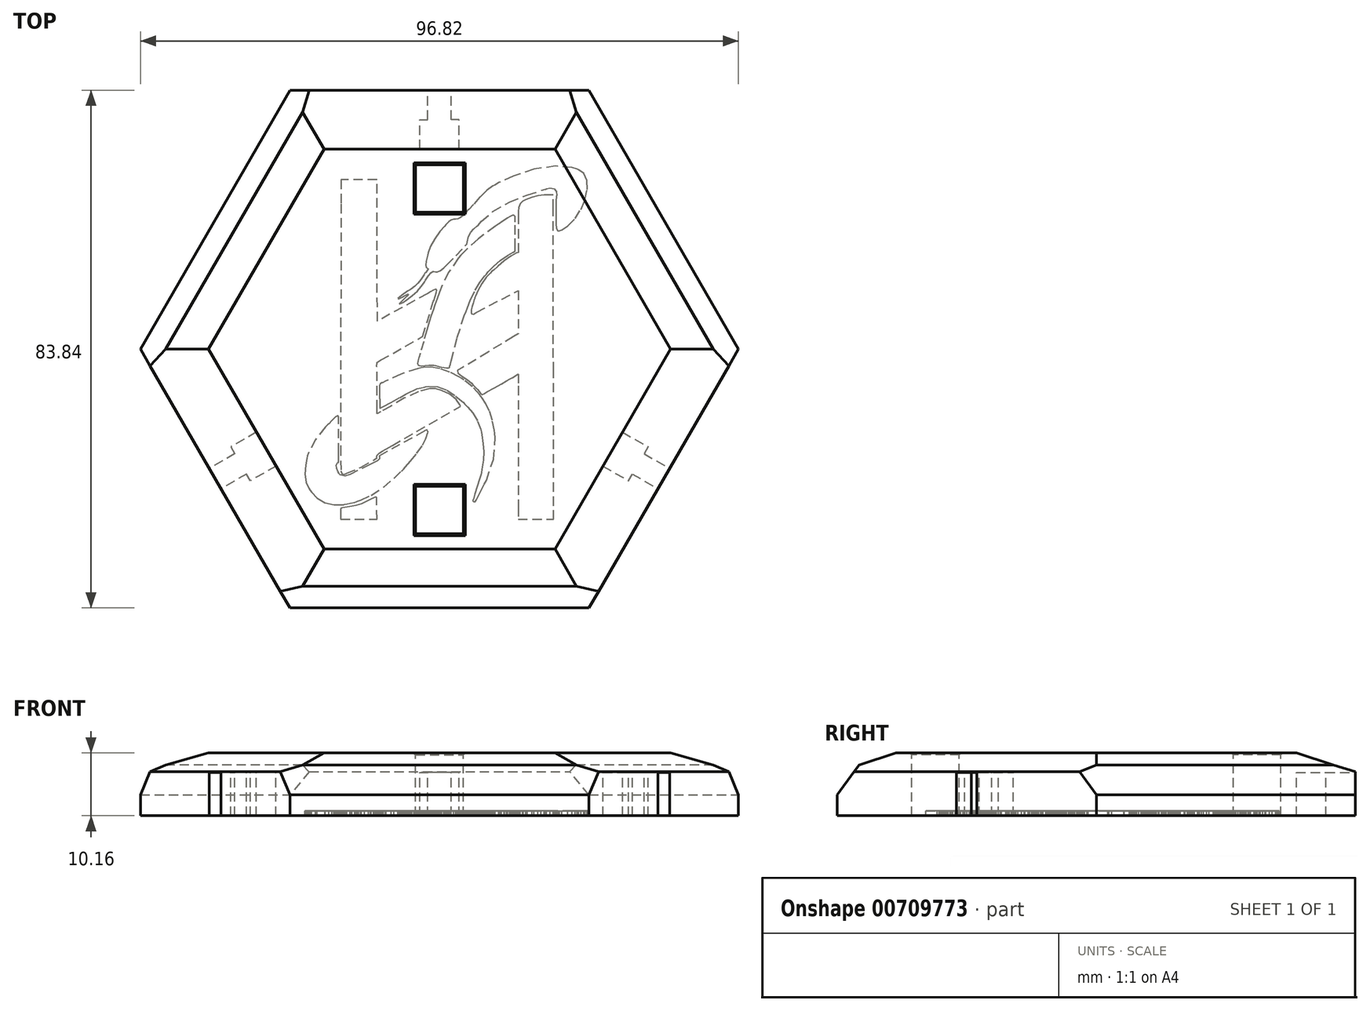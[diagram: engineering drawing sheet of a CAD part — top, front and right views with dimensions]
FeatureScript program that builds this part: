
annotation { "Feature Type Name" : "Feature", "Feature Type Description" : "" }
export const myFeature = defineFeature(function(context is Context, id is Id, definition is map)
    precondition{}
    {
        {
            var Q0;
            Q0=qCreatedBy(makeId("Top.planeOp"),FACE);
            var sketch = newSketch(context, id + "F0", { "sketchPlane" : qUnion([Q0])});
            skLineSegment(sketch, "E0", {"start": v(-18.44, -1.4) * mm, "end": v(-18.44, 0.8) * mm});
            skLineSegment(sketch, "E1", {"start": v(-18.44, 0.8) * mm, "end": v(-18.42, 22.77) * mm});
            skLineSegment(sketch, "E2", {"start": v(-18.42, 22.77) * mm, "end": v(-18.4, 24.97) * mm});
            skLineSegment(sketch, "E3", {"start": v(-18.4, 24.97) * mm, "end": v(-18.04, 24.97) * mm});
            skLineSegment(sketch, "E4", {"start": v(-18.04, 24.97) * mm, "end": v(-16.92, 24.95) * mm});
            skLineSegment(sketch, "E5", {"start": v(-16.92, 24.95) * mm, "end": v(-15.91, 24.86) * mm});
            skLineSegment(sketch, "E6", {"start": v(-15.91, 24.86) * mm, "end": v(-14.95, 24.59) * mm});
            skLineSegment(sketch, "E7", {"start": v(-14.95, 24.59) * mm, "end": v(-13.94, 24.18) * mm});
            skLineSegment(sketch, "E8", {"start": v(-13.94, 24.18) * mm, "end": v(-13.6, 24.04) * mm});
            skLineSegment(sketch, "E9", {"start": v(-13.6, 24.04) * mm, "end": v(-13.45, 23.96) * mm});
            skLineSegment(sketch, "E10", {"start": v(-13.45, 23.96) * mm, "end": v(-13.07, 23.56) * mm});
            skLineSegment(sketch, "E11", {"start": v(-13.07, 23.56) * mm, "end": v(-12.83, 22.93) * mm});
            skLineSegment(sketch, "E12", {"start": v(-12.83, 22.93) * mm, "end": v(-12.77, 22.28) * mm});
            skLineSegment(sketch, "E13", {"start": v(-12.77, 22.28) * mm, "end": v(-12.78, 21.88) * mm});
            skLineSegment(sketch, "E14", {"start": v(-12.78, 21.88) * mm, "end": v(-12.77, 21.74) * mm});
            skLineSegment(sketch, "E15", {"start": v(-12.77, 21.74) * mm, "end": v(-12.77, 15.65) * mm});
            skLineSegment(sketch, "E16", {"start": v(-12.77, 15.65) * mm, "end": v(-12.46, 15.54) * mm});
            skLineSegment(sketch, "E17", {"start": v(-12.46, 15.54) * mm, "end": v(-11.56, 15.07) * mm});
            skLineSegment(sketch, "E18", {"start": v(-11.56, 15.07) * mm, "end": v(-10.49, 14.3) * mm});
            skLineSegment(sketch, "E19", {"start": v(-10.49, 14.3) * mm, "end": v(-9.48, 13.42) * mm});
            skLineSegment(sketch, "E20", {"start": v(-9.48, 13.42) * mm, "end": v(-8.73, 12.77) * mm});
            skLineSegment(sketch, "E21", {"start": v(-8.73, 12.77) * mm, "end": v(-8.47, 12.56) * mm});
            skLineSegment(sketch, "E22", {"start": v(-8.47, 12.56) * mm, "end": v(-8.23, 12.35) * mm});
            skLineSegment(sketch, "E23", {"start": v(-8.23, 12.35) * mm, "end": v(-7.57, 11.64) * mm});
            skLineSegment(sketch, "E24", {"start": v(-7.57, 11.64) * mm, "end": v(-6.85, 10.6) * mm});
            skLineSegment(sketch, "E25", {"start": v(-6.85, 10.6) * mm, "end": v(-6.25, 9.47) * mm});
            skLineSegment(sketch, "E26", {"start": v(-6.25, 9.47) * mm, "end": v(-5.85, 8.6) * mm});
            skLineSegment(sketch, "E27", {"start": v(-5.85, 8.6) * mm, "end": v(-5.73, 8.3) * mm});
            skLineSegment(sketch, "E28", {"start": v(-5.73, 8.3) * mm, "end": v(-5.7, 8.2) * mm});
            skLineSegment(sketch, "E29", {"start": v(-5.7, 8.2) * mm, "end": v(-5.6, 7.92) * mm});
            skLineSegment(sketch, "E30", {"start": v(-5.6, 7.92) * mm, "end": v(-5.43, 7.42) * mm});
            skLineSegment(sketch, "E31", {"start": v(-5.43, 7.42) * mm, "end": v(-5.27, 6.87) * mm});
            skLineSegment(sketch, "E32", {"start": v(-5.27, 6.87) * mm, "end": v(-5.14, 6.36) * mm});
            skLineSegment(sketch, "E33", {"start": v(-5.14, 6.36) * mm, "end": v(-5.11, 5.94) * mm});
            skLineSegment(sketch, "E34", {"start": v(-5.11, 5.94) * mm, "end": v(-5.21, 5.7) * mm});
            skLineSegment(sketch, "E35", {"start": v(-5.21, 5.7) * mm, "end": v(-5.5, 5.69) * mm});
            skLineSegment(sketch, "E36", {"start": v(-5.5, 5.69) * mm, "end": v(-5.9, 5.9) * mm});
            skLineSegment(sketch, "E37", {"start": v(-5.9, 5.9) * mm, "end": v(-6, 6) * mm});
            skLineSegment(sketch, "E38", {"start": v(-6, 6) * mm, "end": v(-12.77, 9.46) * mm});
            skLineSegment(sketch, "E39", {"start": v(-12.77, 9.46) * mm, "end": v(-12.77, 2.48) * mm});
            skLineSegment(sketch, "E40", {"start": v(-12.77, 2.48) * mm, "end": v(-11.97, 2.02) * mm});
            skLineSegment(sketch, "E41", {"start": v(-11.97, 2.02) * mm, "end": v(-7.85, -0.48) * mm});
            skLineSegment(sketch, "E42", {"start": v(-7.85, -0.48) * mm, "end": v(-3.73, -3) * mm});
            skLineSegment(sketch, "E43", {"start": v(-3.73, -3) * mm, "end": v(-2.93, -3.45) * mm});
            skLineSegment(sketch, "E44", {"start": v(-2.93, -3.45) * mm, "end": v(-2.88, -3.5) * mm});
            skLineSegment(sketch, "E45", {"start": v(-2.88, -3.5) * mm, "end": v(-3, -3.86) * mm});
            skLineSegment(sketch, "E46", {"start": v(-3, -3.86) * mm, "end": v(-3.61, -4.35) * mm});
            skLineSegment(sketch, "E47", {"start": v(-3.61, -4.35) * mm, "end": v(-4.5, -4.97) * mm});
            skLineSegment(sketch, "E48", {"start": v(-4.5, -4.97) * mm, "end": v(-5.2, -5.53) * mm});
            skLineSegment(sketch, "E49", {"start": v(-5.2, -5.53) * mm, "end": v(-5.4, -5.75) * mm});
            skLineSegment(sketch, "E50", {"start": v(-5.4, -5.75) * mm, "end": v(-5.6, -5.93) * mm});
            skLineSegment(sketch, "E51", {"start": v(-5.6, -5.93) * mm, "end": v(-6.13, -6.53) * mm});
            skLineSegment(sketch, "E52", {"start": v(-6.13, -6.53) * mm, "end": v(-6.6, -7.1) * mm});
            skLineSegment(sketch, "E53", {"start": v(-6.6, -7.1) * mm, "end": v(-6.94, -7.33) * mm});
            skLineSegment(sketch, "E54", {"start": v(-6.94, -7.33) * mm, "end": v(-7.24, -7.2) * mm});
            skLineSegment(sketch, "E55", {"start": v(-7.24, -7.2) * mm, "end": v(-7.3, -7.14) * mm});
            skLineSegment(sketch, "E56", {"start": v(-7.3, -7.14) * mm, "end": v(-7.7, -6.92) * mm});
            skLineSegment(sketch, "E57", {"start": v(-7.7, -6.92) * mm, "end": v(-8.9, -6.26) * mm});
            skLineSegment(sketch, "E58", {"start": v(-8.9, -6.26) * mm, "end": v(-10.06, -5.62) * mm});
            skLineSegment(sketch, "E59", {"start": v(-10.06, -5.62) * mm, "end": v(-10.87, -5.16) * mm});
            skLineSegment(sketch, "E60", {"start": v(-10.87, -5.16) * mm, "end": v(-11.43, -4.84) * mm});
            skLineSegment(sketch, "E61", {"start": v(-11.43, -4.84) * mm, "end": v(-11.8, -4.61) * mm});
            skLineSegment(sketch, "E62", {"start": v(-11.8, -4.61) * mm, "end": v(-12.1, -4.43) * mm});
            skLineSegment(sketch, "E63", {"start": v(-12.1, -4.43) * mm, "end": v(-12.4, -4.25) * mm});
            skLineSegment(sketch, "E64", {"start": v(-12.4, -4.25) * mm, "end": v(-12.68, -4.08) * mm});
            skLineSegment(sketch, "E65", {"start": v(-12.68, -4.08) * mm, "end": v(-12.77, -4.03) * mm});
            skLineSegment(sketch, "E66", {"start": v(-12.77, -4.03) * mm, "end": v(-12.77, -6) * mm});
            skLineSegment(sketch, "E67", {"start": v(-12.77, -6) * mm, "end": v(-12.75, -25.61) * mm});
            skLineSegment(sketch, "E68", {"start": v(-12.75, -25.61) * mm, "end": v(-12.75, -27.57) * mm});
            skLineSegment(sketch, "E69", {"start": v(-12.75, -27.57) * mm, "end": v(-18.45, -27.57) * mm});
            skLineSegment(sketch, "E70", {"start": v(-18.45, -27.57) * mm, "end": v(-18.45, -25.39) * mm});
            skLineSegment(sketch, "E71", {"start": v(-18.45, -25.39) * mm, "end": v(-18.44, -3.57) * mm});
            skLineSegment(sketch, "E72", {"start": v(-18.44, -3.57) * mm, "end": v(-18.44, -1.4) * mm});
            skLineSegment(sketch, "E73", {"start": v(10.16, -24.07) * mm, "end": v(10.2, -24.02) * mm});
            skLineSegment(sketch, "E74", {"start": v(10.2, -24.02) * mm, "end": v(10.42, -23.96) * mm});
            skLineSegment(sketch, "E75", {"start": v(10.42, -23.96) * mm, "end": v(10.62, -24.06) * mm});
            skLineSegment(sketch, "E76", {"start": v(10.62, -24.06) * mm, "end": v(10.67, -24.09) * mm});
            skLineSegment(sketch, "E77", {"start": v(10.67, -24.09) * mm, "end": v(10.87, -24.2) * mm});
            skLineSegment(sketch, "E78", {"start": v(10.87, -24.2) * mm, "end": v(11.5, -24.52) * mm});
            skLineSegment(sketch, "E79", {"start": v(11.5, -24.52) * mm, "end": v(12.12, -24.83) * mm});
            skLineSegment(sketch, "E80", {"start": v(12.12, -24.83) * mm, "end": v(12.62, -25.06) * mm});
            skLineSegment(sketch, "E81", {"start": v(12.62, -25.06) * mm, "end": v(13.08, -25.22) * mm});
            skLineSegment(sketch, "E82", {"start": v(13.08, -25.22) * mm, "end": v(13.56, -25.34) * mm});
            skLineSegment(sketch, "E83", {"start": v(13.56, -25.34) * mm, "end": v(14.16, -25.46) * mm});
            skLineSegment(sketch, "E84", {"start": v(14.16, -25.46) * mm, "end": v(14.93, -25.6) * mm});
            skLineSegment(sketch, "E85", {"start": v(14.93, -25.6) * mm, "end": v(15.71, -25.74) * mm});
            skLineSegment(sketch, "E86", {"start": v(15.71, -25.74) * mm, "end": v(15.97, -25.78) * mm});
            skLineSegment(sketch, "E87", {"start": v(15.97, -25.78) * mm, "end": v(15.98, -25.98) * mm});
            skLineSegment(sketch, "E88", {"start": v(15.98, -25.98) * mm, "end": v(15.99, -26.56) * mm});
            skLineSegment(sketch, "E89", {"start": v(15.99, -26.56) * mm, "end": v(15.99, -26.68) * mm});
            skLineSegment(sketch, "E90", {"start": v(15.99, -26.68) * mm, "end": v(15.99, -26.79) * mm});
            skLineSegment(sketch, "E91", {"start": v(15.99, -26.79) * mm, "end": v(16, -27.38) * mm});
            skLineSegment(sketch, "E92", {"start": v(16, -27.38) * mm, "end": v(16, -27.57) * mm});
            skLineSegment(sketch, "E93", {"start": v(16, -27.57) * mm, "end": v(10.13, -27.57) * mm});
            skLineSegment(sketch, "E94", {"start": v(10.13, -27.57) * mm, "end": v(10.16, -24.07) * mm});
            skLineSegment(sketch, "E95", {"start": v(13.28, -24.66) * mm, "end": v(12.7, -24.46) * mm});
            skLineSegment(sketch, "E96", {"start": v(12.7, -24.46) * mm, "end": v(11.04, -23.66) * mm});
            skLineSegment(sketch, "E97", {"start": v(11.04, -23.66) * mm, "end": v(9.09, -22.38) * mm});
            skLineSegment(sketch, "E98", {"start": v(9.09, -22.38) * mm, "end": v(7.36, -20.93) * mm});
            skLineSegment(sketch, "E99", {"start": v(7.36, -20.93) * mm, "end": v(6.18, -19.81) * mm});
            skLineSegment(sketch, "E100", {"start": v(6.18, -19.81) * mm, "end": v(5.8, -19.44) * mm});
            skLineSegment(sketch, "E101", {"start": v(5.8, -19.44) * mm, "end": v(5.53, -19.12) * mm});
            skLineSegment(sketch, "E102", {"start": v(5.53, -19.12) * mm, "end": v(4.72, -18.18) * mm});
            skLineSegment(sketch, "E103", {"start": v(4.72, -18.18) * mm, "end": v(3.67, -16.88) * mm});
            skLineSegment(sketch, "E104", {"start": v(3.67, -16.88) * mm, "end": v(2.75, -15.54) * mm});
            skLineSegment(sketch, "E105", {"start": v(2.75, -15.54) * mm, "end": v(2.22, -14.52) * mm});
            skLineSegment(sketch, "E106", {"start": v(2.22, -14.52) * mm, "end": v(2.1, -14.15) * mm});
            skLineSegment(sketch, "E107", {"start": v(2.1, -14.15) * mm, "end": v(2.05, -14.05) * mm});
            skLineSegment(sketch, "E108", {"start": v(2.05, -14.05) * mm, "end": v(1.96, -13.73) * mm});
            skLineSegment(sketch, "E109", {"start": v(1.92, -13.3) * mm, "end": v(2.06, -13.09) * mm});
            skLineSegment(sketch, "E110", {"start": v(2.06, -13.09) * mm, "end": v(2.35, -13.21) * mm});
            skLineSegment(sketch, "E111", {"start": v(2.35, -13.21) * mm, "end": v(2.43, -13.28) * mm});
            skLineSegment(sketch, "E112", {"start": v(2.43, -13.28) * mm, "end": v(9.8, -17.32) * mm});
            skLineSegment(sketch, "E113", {"start": v(9.8, -17.32) * mm, "end": v(9.75, -17.42) * mm});
            skLineSegment(sketch, "E114", {"start": v(9.75, -17.42) * mm, "end": v(9.75, -17.79) * mm});
            skLineSegment(sketch, "E115", {"start": v(9.75, -17.79) * mm, "end": v(10.03, -18.09) * mm});
            skLineSegment(sketch, "E116", {"start": v(10.03, -18.09) * mm, "end": v(10.55, -18.35) * mm});
            skLineSegment(sketch, "E117", {"start": v(10.55, -18.35) * mm, "end": v(11.05, -18.6) * mm});
            skLineSegment(sketch, "E118", {"start": v(11.05, -18.6) * mm, "end": v(11.2, -18.69) * mm});
            skLineSegment(sketch, "E119", {"start": v(11.2, -18.69) * mm, "end": v(14.33, -20.23) * mm});
            skLineSegment(sketch, "E120", {"start": v(14.33, -20.23) * mm, "end": v(14.47, -20.32) * mm});
            skLineSegment(sketch, "E121", {"start": v(14.47, -20.32) * mm, "end": v(15.29, -20.57) * mm});
            skLineSegment(sketch, "E122", {"start": v(15.29, -20.57) * mm, "end": v(16.07, -20.37) * mm});
            skLineSegment(sketch, "E123", {"start": v(16.07, -20.37) * mm, "end": v(16.2, -20.24) * mm});
            skLineSegment(sketch, "E124", {"start": v(16.2, -20.24) * mm, "end": v(16.26, -20.12) * mm});
            skLineSegment(sketch, "E125", {"start": v(16.26, -20.12) * mm, "end": v(16.43, -19.78) * mm});
            skLineSegment(sketch, "E126", {"start": v(16.43, -19.78) * mm, "end": v(16.63, -19.29) * mm});
            skLineSegment(sketch, "E127", {"start": v(16.63, -19.29) * mm, "end": v(16.69, -18.8) * mm});
            skLineSegment(sketch, "E128", {"start": v(16.69, -18.8) * mm, "end": v(16.54, -18.43) * mm});
            skLineSegment(sketch, "E129", {"start": v(16.54, -18.43) * mm, "end": v(16.46, -18.34) * mm});
            skLineSegment(sketch, "E130", {"start": v(16.46, -18.34) * mm, "end": v(16.44, -18.33) * mm});
            skLineSegment(sketch, "E131", {"start": v(16.44, -18.33) * mm, "end": v(16.36, -18.34) * mm});
            skLineSegment(sketch, "E132", {"start": v(16.36, -18.34) * mm, "end": v(16.34, -18.33) * mm});
            skLineSegment(sketch, "E133", {"start": v(16.34, -18.33) * mm, "end": v(16.34, -18.04) * mm});
            skLineSegment(sketch, "E134", {"start": v(16.34, -18.04) * mm, "end": v(16.33, -17.45) * mm});
            skLineSegment(sketch, "E135", {"start": v(16.33, -17.45) * mm, "end": v(16.32, -17.25) * mm});
            skLineSegment(sketch, "E136", {"start": v(16.32, -17.25) * mm, "end": v(16.32, -16.74) * mm});
            skLineSegment(sketch, "E137", {"start": v(16.32, -16.74) * mm, "end": v(16.34, -11.6) * mm});
            skLineSegment(sketch, "E138", {"start": v(16.34, -11.6) * mm, "end": v(16.34, -11.08) * mm});
            skLineSegment(sketch, "E139", {"start": v(16.34, -11.08) * mm, "end": v(16.34, -11) * mm});
            skLineSegment(sketch, "E140", {"start": v(16.34, -11) * mm, "end": v(16.47, -10.76) * mm});
            skLineSegment(sketch, "E141", {"start": v(16.47, -10.76) * mm, "end": v(16.82, -10.97) * mm});
            skLineSegment(sketch, "E142", {"start": v(16.82, -10.97) * mm, "end": v(17.38, -11.54) * mm});
            skLineSegment(sketch, "E143", {"start": v(17.38, -11.54) * mm, "end": v(17.9, -12.1) * mm});
            skLineSegment(sketch, "E144", {"start": v(17.9, -12.1) * mm, "end": v(18.1, -12.27) * mm});
            skLineSegment(sketch, "E145", {"start": v(18.1, -12.27) * mm, "end": v(18.48, -12.65) * mm});
            skLineSegment(sketch, "E146", {"start": v(18.48, -12.65) * mm, "end": v(20.07, -14.64) * mm});
            skLineSegment(sketch, "E147", {"start": v(20.07, -14.64) * mm, "end": v(21.21, -16.83) * mm});
            skLineSegment(sketch, "E148", {"start": v(21.21, -16.83) * mm, "end": v(21.38, -17.3) * mm});
            skLineSegment(sketch, "E149", {"start": v(21.38, -17.3) * mm, "end": v(21.47, -17.68) * mm});
            skLineSegment(sketch, "E150", {"start": v(21.47, -17.68) * mm, "end": v(21.68, -18.8) * mm});
            skLineSegment(sketch, "E151", {"start": v(21.68, -18.8) * mm, "end": v(21.78, -20.22) * mm});
            skLineSegment(sketch, "E152", {"start": v(21.78, -20.22) * mm, "end": v(21.58, -21.57) * mm});
            skLineSegment(sketch, "E153", {"start": v(21.58, -21.57) * mm, "end": v(21.14, -22.56) * mm});
            skLineSegment(sketch, "E154", {"start": v(21.14, -22.56) * mm, "end": v(20.93, -22.84) * mm});
            skLineSegment(sketch, "E155", {"start": v(20.93, -22.84) * mm, "end": v(20.7, -23.2) * mm});
            skLineSegment(sketch, "E156", {"start": v(20.7, -23.2) * mm, "end": v(19.82, -24.12) * mm});
            skLineSegment(sketch, "E157", {"start": v(19.82, -24.12) * mm, "end": v(18.52, -24.9) * mm});
            skLineSegment(sketch, "E158", {"start": v(18.52, -24.9) * mm, "end": v(17.08, -25.22) * mm});
            skLineSegment(sketch, "E159", {"start": v(17.08, -25.22) * mm, "end": v(15.88, -25.22) * mm});
            skLineSegment(sketch, "E160", {"start": v(15.88, -25.22) * mm, "end": v(15.48, -25.17) * mm});
            skLineSegment(sketch, "E161", {"start": v(15.48, -25.17) * mm, "end": v(15.38, -25.15) * mm});
            skLineSegment(sketch, "E162", {"start": v(15.38, -25.15) * mm, "end": v(15.02, -25.09) * mm});
            skLineSegment(sketch, "E163", {"start": v(15.02, -25.09) * mm, "end": v(14.39, -24.96) * mm});
            skLineSegment(sketch, "E164", {"start": v(14.39, -24.96) * mm, "end": v(13.75, -24.81) * mm});
            skLineSegment(sketch, "E165", {"start": v(13.75, -24.81) * mm, "end": v(13.39, -24.7) * mm});
            skLineSegment(sketch, "E166", {"start": v(13.39, -24.7) * mm, "end": v(13.28, -24.66) * mm});
            skLineSegment(sketch, "E167", {"start": v(-5.85, -24.66) * mm, "end": v(-5.98, -24.44) * mm});
            skLineSegment(sketch, "E168", {"start": v(-5.98, -24.44) * mm, "end": v(-6.55, -23.28) * mm});
            skLineSegment(sketch, "E169", {"start": v(-6.55, -23.28) * mm, "end": v(-7.13, -22.13) * mm});
            skLineSegment(sketch, "E170", {"start": v(-7.13, -22.13) * mm, "end": v(-7.27, -21.91) * mm});
            skLineSegment(sketch, "E171", {"start": v(-7.27, -21.91) * mm, "end": v(-7.58, -21.23) * mm});
            skLineSegment(sketch, "E172", {"start": v(-7.58, -21.23) * mm, "end": v(-8.73, -17.82) * mm});
            skLineSegment(sketch, "E173", {"start": v(-8.73, -17.82) * mm, "end": v(-9.04, -14.37) * mm});
            skLineSegment(sketch, "E174", {"start": v(-9.04, -14.37) * mm, "end": v(-8.94, -13.67) * mm});
            skLineSegment(sketch, "E175", {"start": v(-8.94, -13.67) * mm, "end": v(-8.87, -13.14) * mm});
            skLineSegment(sketch, "E176", {"start": v(-8.87, -13.14) * mm, "end": v(-8.56, -11.54) * mm});
            skLineSegment(sketch, "E177", {"start": v(-8.56, -11.54) * mm, "end": v(-8.08, -10) * mm});
            skLineSegment(sketch, "E178", {"start": v(-8.08, -10) * mm, "end": v(-7.47, -8.8) * mm});
            skLineSegment(sketch, "E179", {"start": v(-7.47, -8.8) * mm, "end": v(-6.9, -7.95) * mm});
            skLineSegment(sketch, "E180", {"start": v(-6.9, -7.95) * mm, "end": v(-6.7, -7.68) * mm});
            skLineSegment(sketch, "E181", {"start": v(-6.7, -7.68) * mm, "end": v(-6.5, -7.4) * mm});
            skLineSegment(sketch, "E182", {"start": v(-6.5, -7.4) * mm, "end": v(-5.3, -6.1) * mm});
            skLineSegment(sketch, "E183", {"start": v(-5.3, -6.1) * mm, "end": v(-3.92, -4.98) * mm});
            skLineSegment(sketch, "E184", {"start": v(-3.92, -4.98) * mm, "end": v(-3.64, -4.78) * mm});
            skLineSegment(sketch, "E185", {"start": v(-3.64, -4.78) * mm, "end": v(-3.15, -4.5) * mm});
            skLineSegment(sketch, "E186", {"start": v(-3.15, -4.5) * mm, "end": v(-1.66, -3.75) * mm});
            skLineSegment(sketch, "E187", {"start": v(-1.66, -3.75) * mm, "end": v(-0.05, -3.15) * mm});
            skLineSegment(sketch, "E188", {"start": v(-0.05, -3.15) * mm, "end": v(1.41, -2.93) * mm});
            skLineSegment(sketch, "E189", {"start": v(1.41, -2.93) * mm, "end": v(2.58, -3) * mm});
            skLineSegment(sketch, "E190", {"start": v(2.58, -3) * mm, "end": v(2.97, -3.06) * mm});
            skLineSegment(sketch, "E191", {"start": v(2.97, -3.06) * mm, "end": v(3.52, -3.15) * mm});
            skLineSegment(sketch, "E192", {"start": v(3.52, -3.15) * mm, "end": v(6.24, -4.04) * mm});
            skLineSegment(sketch, "E193", {"start": v(6.24, -4.04) * mm, "end": v(8.78, -5.22) * mm});
            skLineSegment(sketch, "E194", {"start": v(8.78, -5.22) * mm, "end": v(9.24, -5.45) * mm});
            skLineSegment(sketch, "E195", {"start": v(9.24, -5.45) * mm, "end": v(9.33, -5.46) * mm});
            skLineSegment(sketch, "E196", {"start": v(9.33, -5.46) * mm, "end": v(9.6, -5.62) * mm});
            skLineSegment(sketch, "E197", {"start": v(9.6, -5.62) * mm, "end": v(9.73, -5.92) * mm});
            skLineSegment(sketch, "E198", {"start": v(9.73, -5.92) * mm, "end": v(9.74, -6.29) * mm});
            skLineSegment(sketch, "E199", {"start": v(9.74, -6.29) * mm, "end": v(9.73, -6.58) * mm});
            skLineSegment(sketch, "E200", {"start": v(9.73, -6.58) * mm, "end": v(9.74, -6.68) * mm});
            skLineSegment(sketch, "E201", {"start": v(9.74, -6.68) * mm, "end": v(9.73, -6.89) * mm});
            skLineSegment(sketch, "E202", {"start": v(9.73, -6.89) * mm, "end": v(9.7, -7.51) * mm});
            skLineSegment(sketch, "E203", {"start": v(9.7, -7.51) * mm, "end": v(9.69, -7.94) * mm});
            skLineSegment(sketch, "E204", {"start": v(9.69, -7.94) * mm, "end": v(9.68, -8.1) * mm});
            skLineSegment(sketch, "E205", {"start": v(9.68, -8.1) * mm, "end": v(9.68, -8.12) * mm});
            skLineSegment(sketch, "E206", {"start": v(9.68, -8.12) * mm, "end": v(9.68, -8.14) * mm});
            skLineSegment(sketch, "E207", {"start": v(9.68, -8.14) * mm, "end": v(9.68, -8.3) * mm});
            skLineSegment(sketch, "E208", {"start": v(9.68, -8.3) * mm, "end": v(9.66, -8.73) * mm});
            skLineSegment(sketch, "E209", {"start": v(9.66, -8.73) * mm, "end": v(9.64, -9.35) * mm});
            skLineSegment(sketch, "E210", {"start": v(9.64, -9.35) * mm, "end": v(9.63, -9.56) * mm});
            skLineSegment(sketch, "E211", {"start": v(9.63, -9.56) * mm, "end": v(9.17, -9.32) * mm});
            skLineSegment(sketch, "E212", {"start": v(9.17, -9.32) * mm, "end": v(7.79, -8.6) * mm});
            skLineSegment(sketch, "E213", {"start": v(7.79, -8.6) * mm, "end": v(6.43, -7.87) * mm});
            skLineSegment(sketch, "E214", {"start": v(6.43, -7.87) * mm, "end": v(5.44, -7.32) * mm});
            skLineSegment(sketch, "E215", {"start": v(5.44, -7.32) * mm, "end": v(4.72, -6.92) * mm});
            skLineSegment(sketch, "E216", {"start": v(4.72, -6.92) * mm, "end": v(4.14, -6.63) * mm});
            skLineSegment(sketch, "E217", {"start": v(4.14, -6.63) * mm, "end": v(3.6, -6.42) * mm});
            skLineSegment(sketch, "E218", {"start": v(3.6, -6.42) * mm, "end": v(3, -6.25) * mm});
            skLineSegment(sketch, "E219", {"start": v(3, -6.25) * mm, "end": v(2.4, -6.12) * mm});
            skLineSegment(sketch, "E220", {"start": v(2.4, -6.12) * mm, "end": v(2.2, -6.09) * mm});
            skLineSegment(sketch, "E221", {"start": v(2.2, -6.09) * mm, "end": v(1.76, -6.01) * mm});
            skLineSegment(sketch, "E222", {"start": v(1.76, -6.01) * mm, "end": v(0.35, -6.1) * mm});
            skLineSegment(sketch, "E223", {"start": v(0.35, -6.1) * mm, "end": v(-1.23, -6.68) * mm});
            skLineSegment(sketch, "E224", {"start": v(-1.23, -6.68) * mm, "end": v(-2.61, -7.6) * mm});
            skLineSegment(sketch, "E225", {"start": v(-2.61, -7.6) * mm, "end": v(-3.58, -8.39) * mm});
            skLineSegment(sketch, "E226", {"start": v(-3.58, -8.39) * mm, "end": v(-3.9, -8.65) * mm});
            skLineSegment(sketch, "E227", {"start": v(-3.9, -8.65) * mm, "end": v(-4.06, -8.85) * mm});
            skLineSegment(sketch, "E228", {"start": v(-4.06, -8.85) * mm, "end": v(-4.6, -9.41) * mm});
            skLineSegment(sketch, "E229", {"start": v(-4.6, -9.41) * mm, "end": v(-5.4, -10.36) * mm});
            skLineSegment(sketch, "E230", {"start": v(-5.4, -10.36) * mm, "end": v(-6.17, -11.65) * mm});
            skLineSegment(sketch, "E231", {"start": v(-6.17, -11.65) * mm, "end": v(-6.68, -12.97) * mm});
            skLineSegment(sketch, "E232", {"start": v(-6.68, -12.97) * mm, "end": v(-6.8, -13.43) * mm});
            skLineSegment(sketch, "E233", {"start": v(-6.8, -13.43) * mm, "end": v(-6.86, -13.9) * mm});
            skLineSegment(sketch, "E234", {"start": v(-6.86, -13.9) * mm, "end": v(-7.05, -15.31) * mm});
            skLineSegment(sketch, "E235", {"start": v(-7.05, -15.31) * mm, "end": v(-7.15, -16.62) * mm});
            skLineSegment(sketch, "E236", {"start": v(-7.15, -16.62) * mm, "end": v(-7.08, -17.98) * mm});
            skLineSegment(sketch, "E237", {"start": v(-7.08, -17.98) * mm, "end": v(-6.87, -19.51) * mm});
            skLineSegment(sketch, "E238", {"start": v(-6.87, -19.51) * mm, "end": v(-6.79, -20.02) * mm});
            skLineSegment(sketch, "E239", {"start": v(-6.79, -20.02) * mm, "end": v(-6.71, -20.28) * mm});
            skLineSegment(sketch, "E240", {"start": v(-6.71, -20.28) * mm, "end": v(-6.48, -21.06) * mm});
            skLineSegment(sketch, "E241", {"start": v(-6.48, -21.06) * mm, "end": v(-6.12, -22.27) * mm});
            skLineSegment(sketch, "E242", {"start": v(-6.12, -22.27) * mm, "end": v(-5.74, -23.48) * mm});
            skLineSegment(sketch, "E243", {"start": v(-5.74, -23.48) * mm, "end": v(-5.49, -24.25) * mm});
            skLineSegment(sketch, "E244", {"start": v(-5.49, -24.25) * mm, "end": v(-5.4, -24.5) * mm});
            skLineSegment(sketch, "E245", {"start": v(-5.4, -24.5) * mm, "end": v(-5.4, -24.55) * mm});
            skLineSegment(sketch, "E246", {"start": v(-5.4, -24.55) * mm, "end": v(-5.59, -24.72) * mm});
            skLineSegment(sketch, "E247", {"start": v(-5.59, -24.72) * mm, "end": v(-5.82, -24.7) * mm});
            skLineSegment(sketch, "E248", {"start": v(-5.82, -24.7) * mm, "end": v(-5.85, -24.66) * mm});
            skLineSegment(sketch, "E249", {"start": v(15.52, -20.3) * mm, "end": v(15.05, -20.15) * mm});
            skLineSegment(sketch, "E250", {"start": v(15.05, -20.15) * mm, "end": v(12.75, -19.17) * mm});
            skLineSegment(sketch, "E251", {"start": v(12.75, -19.17) * mm, "end": v(10.53, -17.88) * mm});
            skLineSegment(sketch, "E252", {"start": v(10.53, -17.88) * mm, "end": v(10.11, -17.57) * mm});
            skLineSegment(sketch, "E253", {"start": v(10.11, -17.57) * mm, "end": v(10.16, -17.5) * mm});
            skLineSegment(sketch, "E254", {"start": v(10.16, -17.5) * mm, "end": v(10.12, -17.18) * mm});
            skLineSegment(sketch, "E255", {"start": v(10.12, -17.18) * mm, "end": v(9.75, -16.83) * mm});
            skLineSegment(sketch, "E256", {"start": v(9.75, -16.83) * mm, "end": v(9.2, -16.5) * mm});
            skLineSegment(sketch, "E257", {"start": v(9.2, -16.5) * mm, "end": v(8.8, -16.25) * mm});
            skLineSegment(sketch, "E258", {"start": v(8.8, -16.25) * mm, "end": v(8.66, -16.16) * mm});
            skLineSegment(sketch, "E259", {"start": v(8.66, -16.16) * mm, "end": v(7.66, -15.58) * mm});
            skLineSegment(sketch, "E260", {"start": v(7.66, -15.58) * mm, "end": v(-2.4, -9.86) * mm});
            skLineSegment(sketch, "E261", {"start": v(-2.4, -9.86) * mm, "end": v(-3.4, -9.28) * mm});
            skLineSegment(sketch, "E262", {"start": v(-3.4, -9.28) * mm, "end": v(-3.3, -8.98) * mm});
            skLineSegment(sketch, "E263", {"start": v(-3.3, -8.98) * mm, "end": v(-2.72, -8.17) * mm});
            skLineSegment(sketch, "E264", {"start": v(-2.72, -8.17) * mm, "end": v(-1.65, -7.3) * mm});
            skLineSegment(sketch, "E265", {"start": v(-1.65, -7.3) * mm, "end": v(-0.35, -6.7) * mm});
            skLineSegment(sketch, "E266", {"start": v(-0.35, -6.7) * mm, "end": v(0.64, -6.43) * mm});
            skLineSegment(sketch, "E267", {"start": v(0.64, -6.43) * mm, "end": v(0.97, -6.4) * mm});
            skLineSegment(sketch, "E268", {"start": v(0.97, -6.4) * mm, "end": v(1.6, -6.43) * mm});
            skLineSegment(sketch, "E269", {"start": v(1.6, -6.43) * mm, "end": v(3.43, -6.92) * mm});
            skLineSegment(sketch, "E270", {"start": v(3.43, -6.92) * mm, "end": v(5.72, -7.96) * mm});
            skLineSegment(sketch, "E271", {"start": v(5.72, -7.96) * mm, "end": v(7.91, -9.23) * mm});
            skLineSegment(sketch, "E272", {"start": v(7.91, -9.23) * mm, "end": v(9.55, -10.18) * mm});
            skLineSegment(sketch, "E273", {"start": v(9.55, -10.18) * mm, "end": v(10.12, -10.46) * mm});
            skLineSegment(sketch, "E274", {"start": v(10.12, -10.46) * mm, "end": v(10.13, -9.77) * mm});
            skLineSegment(sketch, "E275", {"start": v(10.13, -9.77) * mm, "end": v(10.13, -2.84) * mm});
            skLineSegment(sketch, "E276", {"start": v(10.13, -2.84) * mm, "end": v(10.13, -2.14) * mm});
            skLineSegment(sketch, "E277", {"start": v(10.13, -2.14) * mm, "end": v(9.5, -1.8) * mm});
            skLineSegment(sketch, "E278", {"start": v(9.5, -1.8) * mm, "end": v(3.33, 1.7) * mm});
            skLineSegment(sketch, "E279", {"start": v(3.33, 1.7) * mm, "end": v(2.71, 2.04) * mm});
            skLineSegment(sketch, "E280", {"start": v(2.71, 2.04) * mm, "end": v(1, 7.7) * mm});
            skLineSegment(sketch, "E281", {"start": v(1, 7.7) * mm, "end": v(0.92, 7.91) * mm});
            skLineSegment(sketch, "E282", {"start": v(0.92, 7.91) * mm, "end": v(0.7, 8.54) * mm});
            skLineSegment(sketch, "E283", {"start": v(0.7, 8.54) * mm, "end": v(0.52, 9.14) * mm});
            skLineSegment(sketch, "E284", {"start": v(0.52, 9.14) * mm, "end": v(0.47, 9.5) * mm});
            skLineSegment(sketch, "E285", {"start": v(0.47, 9.5) * mm, "end": v(0.53, 9.68) * mm});
            skLineSegment(sketch, "E286", {"start": v(0.53, 9.68) * mm, "end": v(0.72, 9.68) * mm});
            skLineSegment(sketch, "E287", {"start": v(0.72, 9.68) * mm, "end": v(1.03, 9.55) * mm});
            skLineSegment(sketch, "E288", {"start": v(1.03, 9.55) * mm, "end": v(1.45, 9.3) * mm});
            skLineSegment(sketch, "E289", {"start": v(1.45, 9.3) * mm, "end": v(1.86, 9.05) * mm});
            skLineSegment(sketch, "E290", {"start": v(1.86, 9.05) * mm, "end": v(2, 8.96) * mm});
            skLineSegment(sketch, "E291", {"start": v(2, 8.96) * mm, "end": v(10.06, 4.53) * mm});
            skLineSegment(sketch, "E292", {"start": v(10.06, 4.53) * mm, "end": v(10.13, 27.43) * mm});
            skLineSegment(sketch, "E293", {"start": v(10.13, 27.43) * mm, "end": v(15.95, 27.43) * mm});
            skLineSegment(sketch, "E294", {"start": v(15.95, 27.43) * mm, "end": v(15.97, 23.49) * mm});
            skLineSegment(sketch, "E295", {"start": v(15.97, 23.49) * mm, "end": v(15.99, -15.76) * mm});
            skLineSegment(sketch, "E296", {"start": v(15.99, -15.76) * mm, "end": v(15.97, -19.71) * mm});
            skLineSegment(sketch, "E297", {"start": v(15.97, -19.71) * mm, "end": v(15.96, -19.77) * mm});
            skLineSegment(sketch, "E298", {"start": v(15.96, -19.77) * mm, "end": v(15.82, -20.1) * mm});
            skLineSegment(sketch, "E299", {"start": v(15.82, -20.1) * mm, "end": v(15.58, -20.3) * mm});
            skLineSegment(sketch, "E300", {"start": v(15.58, -20.3) * mm, "end": v(15.52, -20.3) * mm});
            skLineSegment(sketch, "E301", {"start": v(-1.75, -2.47) * mm, "end": v(-1.89, -1.88) * mm});
            skLineSegment(sketch, "E302", {"start": v(-1.89, -1.88) * mm, "end": v(-2.88, 1.86) * mm});
            skLineSegment(sketch, "E303", {"start": v(-2.88, 1.86) * mm, "end": v(-4, 5.39) * mm});
            skLineSegment(sketch, "E304", {"start": v(-4, 5.39) * mm, "end": v(-4.3, 6.1) * mm});
            skLineSegment(sketch, "E305", {"start": v(-4.3, 6.1) * mm, "end": v(-4.47, 6.59) * mm});
            skLineSegment(sketch, "E306", {"start": v(-4.47, 6.59) * mm, "end": v(-5.04, 8.01) * mm});
            skLineSegment(sketch, "E307", {"start": v(-5.04, 8.01) * mm, "end": v(-5.75, 9.51) * mm});
            skLineSegment(sketch, "E308", {"start": v(-5.75, 9.51) * mm, "end": v(-6.56, 10.82) * mm});
            skLineSegment(sketch, "E309", {"start": v(-6.56, 10.82) * mm, "end": v(-7.32, 11.84) * mm});
            skLineSegment(sketch, "E310", {"start": v(-7.32, 11.84) * mm, "end": v(-7.58, 12.17) * mm});
            skLineSegment(sketch, "E311", {"start": v(-7.58, 12.17) * mm, "end": v(-7.85, 12.5) * mm});
            skLineSegment(sketch, "E312", {"start": v(-7.85, 12.5) * mm, "end": v(-8.73, 13.4) * mm});
            skLineSegment(sketch, "E313", {"start": v(-8.73, 13.4) * mm, "end": v(-9.86, 14.37) * mm});
            skLineSegment(sketch, "E314", {"start": v(-9.86, 14.37) * mm, "end": v(-11.02, 15.17) * mm});
            skLineSegment(sketch, "E315", {"start": v(-11.02, 15.17) * mm, "end": v(-11.95, 15.72) * mm});
            skLineSegment(sketch, "E316", {"start": v(-11.95, 15.72) * mm, "end": v(-12.27, 15.9) * mm});
            skLineSegment(sketch, "E317", {"start": v(-12.27, 15.9) * mm, "end": v(-12.28, 16.41) * mm});
            skLineSegment(sketch, "E318", {"start": v(-12.28, 16.41) * mm, "end": v(-12.28, 18.58) * mm});
            skLineSegment(sketch, "E319", {"start": v(-12.28, 18.58) * mm, "end": v(-12.26, 20.6) * mm});
            skLineSegment(sketch, "E320", {"start": v(-12.26, 20.6) * mm, "end": v(-12.27, 21.05) * mm});
            skLineSegment(sketch, "E321", {"start": v(-12.27, 21.05) * mm, "end": v(-12.27, 21.15) * mm});
            skLineSegment(sketch, "E322", {"start": v(-12.27, 21.15) * mm, "end": v(-12.23, 21.46) * mm});
            skLineSegment(sketch, "E323", {"start": v(-12.23, 21.46) * mm, "end": v(-12.07, 21.64) * mm});
            skLineSegment(sketch, "E324", {"start": v(-12.07, 21.64) * mm, "end": v(-11.8, 21.64) * mm});
            skLineSegment(sketch, "E325", {"start": v(-11.8, 21.64) * mm, "end": v(-11.43, 21.49) * mm});
            skLineSegment(sketch, "E326", {"start": v(-11.43, 21.49) * mm, "end": v(-11, 21.23) * mm});
            skLineSegment(sketch, "E327", {"start": v(-11, 21.23) * mm, "end": v(-10.54, 20.92) * mm});
            skLineSegment(sketch, "E328", {"start": v(-10.54, 20.92) * mm, "end": v(-10.06, 20.58) * mm});
            skLineSegment(sketch, "E329", {"start": v(-10.06, 20.58) * mm, "end": v(-9.7, 20.35) * mm});
            skLineSegment(sketch, "E330", {"start": v(-9.7, 20.35) * mm, "end": v(-9.58, 20.27) * mm});
            skLineSegment(sketch, "E331", {"start": v(-9.58, 20.27) * mm, "end": v(-9.03, 19.9) * mm});
            skLineSegment(sketch, "E332", {"start": v(-9.03, 19.9) * mm, "end": v(-6.27, 17.88) * mm});
            skLineSegment(sketch, "E333", {"start": v(-6.27, 17.88) * mm, "end": v(-3.84, 15.65) * mm});
            skLineSegment(sketch, "E334", {"start": v(-3.84, 15.65) * mm, "end": v(-3.45, 15.16) * mm});
            skLineSegment(sketch, "E335", {"start": v(-3.45, 15.16) * mm, "end": v(-3.06, 14.73) * mm});
            skLineSegment(sketch, "E336", {"start": v(-3.06, 14.73) * mm, "end": v(-1.48, 12.45) * mm});
            skLineSegment(sketch, "E337", {"start": v(-1.48, 12.45) * mm, "end": v(-0.3, 10.04) * mm});
            skLineSegment(sketch, "E338", {"start": v(-0.3, 10.04) * mm, "end": v(-0.1, 9.53) * mm});
            skLineSegment(sketch, "E339", {"start": v(-0.1, 9.53) * mm, "end": v(0.02, 9.19) * mm});
            skLineSegment(sketch, "E340", {"start": v(0.02, 9.19) * mm, "end": v(0.39, 8.16) * mm});
            skLineSegment(sketch, "E341", {"start": v(0.39, 8.16) * mm, "end": v(0.75, 7.14) * mm});
            skLineSegment(sketch, "E342", {"start": v(0.75, 7.14) * mm, "end": v(1.04, 6.3) * mm});
            skLineSegment(sketch, "E343", {"start": v(1.04, 6.3) * mm, "end": v(1.32, 5.47) * mm});
            skLineSegment(sketch, "E344", {"start": v(1.32, 5.47) * mm, "end": v(1.64, 4.46) * mm});
            skLineSegment(sketch, "E345", {"start": v(1.64, 4.46) * mm, "end": v(2.04, 3.11) * mm});
            skLineSegment(sketch, "E346", {"start": v(2.04, 3.11) * mm, "end": v(2.58, 1.24) * mm});
            skLineSegment(sketch, "E347", {"start": v(2.58, 1.24) * mm, "end": v(3.13, -0.69) * mm});
            skLineSegment(sketch, "E348", {"start": v(3.13, -0.69) * mm, "end": v(3.3, -1.33) * mm});
            skLineSegment(sketch, "E349", {"start": v(3.3, -1.33) * mm, "end": v(3.36, -1.48) * mm});
            skLineSegment(sketch, "E350", {"start": v(3.36, -1.48) * mm, "end": v(3.5, -1.94) * mm});
            skLineSegment(sketch, "E351", {"start": v(3.5, -1.94) * mm, "end": v(3.54, -2.33) * mm});
            skLineSegment(sketch, "E352", {"start": v(3.54, -2.33) * mm, "end": v(3.45, -2.57) * mm});
            skLineSegment(sketch, "E353", {"start": v(3.45, -2.57) * mm, "end": v(3.21, -2.67) * mm});
            skLineSegment(sketch, "E354", {"start": v(3.21, -2.67) * mm, "end": v(2.85, -2.7) * mm});
            skLineSegment(sketch, "E355", {"start": v(2.85, -2.7) * mm, "end": v(2.34, -2.66) * mm});
            skLineSegment(sketch, "E356", {"start": v(2.34, -2.66) * mm, "end": v(1.71, -2.62) * mm});
            skLineSegment(sketch, "E357", {"start": v(1.71, -2.62) * mm, "end": v(1.14, -2.61) * mm});
            skLineSegment(sketch, "E358", {"start": v(1.14, -2.61) * mm, "end": v(0.96, -2.62) * mm});
            skLineSegment(sketch, "E359", {"start": v(0.96, -2.62) * mm, "end": v(0.87, -2.62) * mm});
            skLineSegment(sketch, "E360", {"start": v(0.87, -2.62) * mm, "end": v(0.62, -2.66) * mm});
            skLineSegment(sketch, "E361", {"start": v(0.62, -2.66) * mm, "end": v(0.2, -2.76) * mm});
            skLineSegment(sketch, "E362", {"start": v(0.2, -2.76) * mm, "end": v(-0.27, -2.89) * mm});
            skLineSegment(sketch, "E363", {"start": v(-0.27, -2.89) * mm, "end": v(-0.73, -3) * mm});
            skLineSegment(sketch, "E364", {"start": v(-0.73, -3) * mm, "end": v(-1.15, -3.07) * mm});
            skLineSegment(sketch, "E365", {"start": v(-1.15, -3.07) * mm, "end": v(-1.47, -3.07) * mm});
            skLineSegment(sketch, "E366", {"start": v(-1.47, -3.07) * mm, "end": v(-1.65, -2.96) * mm});
            skLineSegment(sketch, "E367", {"start": v(-1.65, -2.96) * mm, "end": v(-1.67, -2.76) * mm});
            skLineSegment(sketch, "E368", {"start": v(-1.67, -2.76) * mm, "end": v(-1.75, -2.47) * mm});
            skLineSegment(sketch, "E369", {"start": v(2.41, 10.89) * mm, "end": v(2.26, 11.14) * mm});
            skLineSegment(sketch, "E370", {"start": v(2.26, 11.14) * mm, "end": v(1.78, 11.88) * mm});
            skLineSegment(sketch, "E371", {"start": v(1.78, 11.88) * mm, "end": v(1.36, 12.4) * mm});
            skLineSegment(sketch, "E372", {"start": v(1.36, 12.4) * mm, "end": v(1.08, 12.6) * mm});
            skLineSegment(sketch, "E373", {"start": v(1.08, 12.6) * mm, "end": v(0.87, 12.59) * mm});
            skLineSegment(sketch, "E374", {"start": v(0.87, 12.59) * mm, "end": v(0.65, 12.51) * mm});
            skLineSegment(sketch, "E375", {"start": v(0.65, 12.51) * mm, "end": v(0.34, 12.52) * mm});
            skLineSegment(sketch, "E376", {"start": v(0.34, 12.52) * mm, "end": v(-0.13, 12.72) * mm});
            skLineSegment(sketch, "E377", {"start": v(-0.13, 12.72) * mm, "end": v(-0.68, 13.13) * mm});
            skLineSegment(sketch, "E378", {"start": v(-0.68, 13.13) * mm, "end": v(-0.85, 13.27) * mm});
            skLineSegment(sketch, "E379", {"start": v(-0.85, 13.27) * mm, "end": v(-1.16, 13.58) * mm});
            skLineSegment(sketch, "E380", {"start": v(-1.16, 13.58) * mm, "end": v(-2.68, 15.11) * mm});
            skLineSegment(sketch, "E381", {"start": v(-2.68, 15.11) * mm, "end": v(-4.14, 16.7) * mm});
            skLineSegment(sketch, "E382", {"start": v(-4.14, 16.7) * mm, "end": v(-4.42, 17.04) * mm});
            skLineSegment(sketch, "E383", {"start": v(-4.42, 17.04) * mm, "end": v(-4.48, 17.34) * mm});
            skLineSegment(sketch, "E384", {"start": v(-4.48, 17.34) * mm, "end": v(-4.72, 18.23) * mm});
            skLineSegment(sketch, "E385", {"start": v(-4.72, 18.23) * mm, "end": v(-5.06, 18.92) * mm});
            skLineSegment(sketch, "E386", {"start": v(-5.06, 18.92) * mm, "end": v(-5.54, 19.44) * mm});
            skLineSegment(sketch, "E387", {"start": v(-5.54, 19.44) * mm, "end": v(-6.1, 19.92) * mm});
            skLineSegment(sketch, "E388", {"start": v(-6.1, 19.92) * mm, "end": v(-6.28, 20.08) * mm});
            skLineSegment(sketch, "E389", {"start": v(-6.28, 20.08) * mm, "end": v(-6.8, 20.7) * mm});
            skLineSegment(sketch, "E390", {"start": v(-6.8, 20.7) * mm, "end": v(-8.65, 22.28) * mm});
            skLineSegment(sketch, "E391", {"start": v(-8.65, 22.28) * mm, "end": v(-11.36, 23.85) * mm});
            skLineSegment(sketch, "E392", {"start": v(-11.36, 23.85) * mm, "end": v(-14.25, 24.98) * mm});
            skLineSegment(sketch, "E393", {"start": v(-14.25, 24.98) * mm, "end": v(-16.43, 25.66) * mm});
            skLineSegment(sketch, "E394", {"start": v(-17.16, 25.87) * mm, "end": v(-17.34, 25.95) * mm});
            skLineSegment(sketch, "E395", {"start": v(-17.34, 25.95) * mm, "end": v(-17.9, 26.08) * mm});
            skLineSegment(sketch, "E396", {"start": v(-17.9, 26.08) * mm, "end": v(-18.52, 25.99) * mm});
            skLineSegment(sketch, "E397", {"start": v(-18.52, 25.99) * mm, "end": v(-18.9, 25.55) * mm});
            skLineSegment(sketch, "E398", {"start": v(-18.9, 25.55) * mm, "end": v(-18.96, 24.91) * mm});
            skLineSegment(sketch, "E399", {"start": v(-18.96, 24.91) * mm, "end": v(-18.93, 24.7) * mm});
            skLineSegment(sketch, "E400", {"start": v(-18.93, 24.7) * mm, "end": v(-18.9, 24.57) * mm});
            skLineSegment(sketch, "E401", {"start": v(-18.9, 24.57) * mm, "end": v(-18.86, 24.14) * mm});
            skLineSegment(sketch, "E402", {"start": v(-18.86, 24.14) * mm, "end": v(-18.85, 23.27) * mm});
            skLineSegment(sketch, "E403", {"start": v(-18.85, 23.27) * mm, "end": v(-18.87, 22.14) * mm});
            skLineSegment(sketch, "E404", {"start": v(-18.87, 22.14) * mm, "end": v(-18.87, 21.14) * mm});
            skLineSegment(sketch, "E405", {"start": v(-18.87, 21.14) * mm, "end": v(-18.86, 20.81) * mm});
            skLineSegment(sketch, "E406", {"start": v(-18.86, 20.81) * mm, "end": v(-18.87, 20.66) * mm});
            skLineSegment(sketch, "E407", {"start": v(-18.87, 20.66) * mm, "end": v(-18.88, 20.2) * mm});
            skLineSegment(sketch, "E408", {"start": v(-18.88, 20.2) * mm, "end": v(-18.92, 19.61) * mm});
            skLineSegment(sketch, "E409", {"start": v(-18.92, 19.61) * mm, "end": v(-19.09, 19.22) * mm});
            skLineSegment(sketch, "E410", {"start": v(-19.09, 19.22) * mm, "end": v(-19.38, 19.15) * mm});
            skLineSegment(sketch, "E411", {"start": v(-19.38, 19.15) * mm, "end": v(-19.46, 19.18) * mm});
            skLineSegment(sketch, "E412", {"start": v(-19.46, 19.18) * mm, "end": v(-19.8, 19.3) * mm});
            skLineSegment(sketch, "E413", {"start": v(-19.8, 19.3) * mm, "end": v(-20.77, 19.96) * mm});
            skLineSegment(sketch, "E414", {"start": v(-20.77, 19.96) * mm, "end": v(-21.94, 21.16) * mm});
            skLineSegment(sketch, "E415", {"start": v(-21.94, 21.16) * mm, "end": v(-22.9, 22.64) * mm});
            skLineSegment(sketch, "E416", {"start": v(-22.9, 22.64) * mm, "end": v(-23.58, 24.26) * mm});
            skLineSegment(sketch, "E417", {"start": v(-23.58, 24.26) * mm, "end": v(-23.93, 25.86) * mm});
            skLineSegment(sketch, "E418", {"start": v(-23.93, 25.86) * mm, "end": v(-23.86, 27.3) * mm});
            skLineSegment(sketch, "E419", {"start": v(-23.86, 27.3) * mm, "end": v(-23.33, 28.45) * mm});
            skLineSegment(sketch, "E420", {"start": v(-23.33, 28.45) * mm, "end": v(-22.56, 29.06) * mm});
            skLineSegment(sketch, "E421", {"start": v(-22.56, 29.06) * mm, "end": v(-22.27, 29.15) * mm});
            skLineSegment(sketch, "E422", {"start": v(-22.27, 29.15) * mm, "end": v(-21.45, 29.41) * mm});
            skLineSegment(sketch, "E423", {"start": v(-21.45, 29.41) * mm, "end": v(-18.8, 29.63) * mm});
            skLineSegment(sketch, "E424", {"start": v(-18.8, 29.63) * mm, "end": v(-15.28, 29.14) * mm});
            skLineSegment(sketch, "E425", {"start": v(-15.28, 29.14) * mm, "end": v(-11.92, 28.01) * mm});
            skLineSegment(sketch, "E426", {"start": v(-11.92, 28.01) * mm, "end": v(-9.68, 26.97) * mm});
            skLineSegment(sketch, "E427", {"start": v(-9.68, 26.97) * mm, "end": v(-8.95, 26.57) * mm});
            skLineSegment(sketch, "E428", {"start": v(-8.95, 26.57) * mm, "end": v(-8.61, 26.4) * mm});
            skLineSegment(sketch, "E429", {"start": v(-8.61, 26.4) * mm, "end": v(-7.67, 25.7) * mm});
            skLineSegment(sketch, "E430", {"start": v(-7.67, 25.7) * mm, "end": v(-6.56, 24.63) * mm});
            skLineSegment(sketch, "E431", {"start": v(-6.56, 24.63) * mm, "end": v(-5.53, 23.47) * mm});
            skLineSegment(sketch, "E432", {"start": v(-5.53, 23.47) * mm, "end": v(-4.74, 22.62) * mm});
            skLineSegment(sketch, "E433", {"start": v(-4.74, 22.62) * mm, "end": v(-4.46, 22.35) * mm});
            skLineSegment(sketch, "E434", {"start": v(-4.46, 22.35) * mm, "end": v(-4.33, 22.17) * mm});
            skLineSegment(sketch, "E435", {"start": v(-4.33, 22.17) * mm, "end": v(-3.87, 21.68) * mm});
            skLineSegment(sketch, "E436", {"start": v(-3.87, 21.68) * mm, "end": v(-3.4, 21.3) * mm});
            skLineSegment(sketch, "E437", {"start": v(-3.4, 21.3) * mm, "end": v(-2.98, 21.12) * mm});
            skLineSegment(sketch, "E438", {"start": v(-2.98, 21.12) * mm, "end": v(-2.62, 21.04) * mm});
            skLineSegment(sketch, "E439", {"start": v(-2.62, 21.04) * mm, "end": v(-2.28, 21) * mm});
            skLineSegment(sketch, "E440", {"start": v(-2.28, 21) * mm, "end": v(-1.92, 20.89) * mm});
            skLineSegment(sketch, "E441", {"start": v(-1.92, 20.89) * mm, "end": v(-1.51, 20.63) * mm});
            skLineSegment(sketch, "E442", {"start": v(-1.51, 20.63) * mm, "end": v(-1.14, 20.26) * mm});
            skLineSegment(sketch, "E443", {"start": v(-1.14, 20.26) * mm, "end": v(-1.03, 20.12) * mm});
            skLineSegment(sketch, "E444", {"start": v(-1.03, 20.12) * mm, "end": v(-0.79, 19.86) * mm});
            skLineSegment(sketch, "E445", {"start": v(-0.79, 19.86) * mm, "end": v(-0.08, 19.04) * mm});
            skLineSegment(sketch, "E446", {"start": v(-0.08, 19.04) * mm, "end": v(0.78, 17.88) * mm});
            skLineSegment(sketch, "E447", {"start": v(0.78, 17.88) * mm, "end": v(1.47, 16.62) * mm});
            skLineSegment(sketch, "E448", {"start": v(1.47, 16.62) * mm, "end": v(1.85, 15.6) * mm});
            skLineSegment(sketch, "E449", {"start": v(1.85, 15.6) * mm, "end": v(1.92, 15.24) * mm});
            skLineSegment(sketch, "E450", {"start": v(1.92, 15.24) * mm, "end": v(2, 15) * mm});
            skLineSegment(sketch, "E451", {"start": v(2, 15) * mm, "end": v(2.19, 14.24) * mm});
            skLineSegment(sketch, "E452", {"start": v(2.19, 14.24) * mm, "end": v(2.24, 13.61) * mm});
            skLineSegment(sketch, "E453", {"start": v(2.24, 13.61) * mm, "end": v(2.15, 13.28) * mm});
            skLineSegment(sketch, "E454", {"start": v(2.15, 13.28) * mm, "end": v(2, 13.12) * mm});
            skLineSegment(sketch, "E455", {"start": v(2, 13.12) * mm, "end": v(1.87, 13.04) * mm});
            skLineSegment(sketch, "E456", {"start": v(1.87, 13.04) * mm, "end": v(1.83, 12.95) * mm});
            skLineSegment(sketch, "E457", {"start": v(1.83, 12.95) * mm, "end": v(1.96, 12.74) * mm});
            skLineSegment(sketch, "E458", {"start": v(1.96, 12.74) * mm, "end": v(2.25, 12.42) * mm});
            skLineSegment(sketch, "E459", {"start": v(2.25, 12.42) * mm, "end": v(2.35, 12.31) * mm});
            skLineSegment(sketch, "E460", {"start": v(2.35, 12.31) * mm, "end": v(2.51, 12.07) * mm});
            skLineSegment(sketch, "E461", {"start": v(2.51, 12.07) * mm, "end": v(3.01, 11.32) * mm});
            skLineSegment(sketch, "E462", {"start": v(3.01, 11.32) * mm, "end": v(3.5, 10.67) * mm});
            skLineSegment(sketch, "E463", {"start": v(3.5, 10.67) * mm, "end": v(4.01, 10.16) * mm});
            skLineSegment(sketch, "E464", {"start": v(4.01, 10.16) * mm, "end": v(4.59, 9.74) * mm});
            skLineSegment(sketch, "E465", {"start": v(4.59, 9.74) * mm, "end": v(4.79, 9.61) * mm});
            skLineSegment(sketch, "E466", {"start": v(4.79, 9.61) * mm, "end": v(5.13, 9.4) * mm});
            skLineSegment(sketch, "E467", {"start": v(5.13, 9.4) * mm, "end": v(6.11, 8.73) * mm});
            skLineSegment(sketch, "E468", {"start": v(6.11, 8.73) * mm, "end": v(6.71, 8.2) * mm});
            skLineSegment(sketch, "E469", {"start": v(6.71, 8.2) * mm, "end": v(6.6, 8.13) * mm});
            skLineSegment(sketch, "E470", {"start": v(6.6, 8.13) * mm, "end": v(6, 8.44) * mm});
            skLineSegment(sketch, "E471", {"start": v(6, 8.44) * mm, "end": v(5.8, 8.56) * mm});
            skLineSegment(sketch, "E472", {"start": v(5.8, 8.56) * mm, "end": v(5.64, 8.66) * mm});
            skLineSegment(sketch, "E473", {"start": v(5.64, 8.66) * mm, "end": v(5.15, 8.92) * mm});
            skLineSegment(sketch, "E474", {"start": v(5.15, 8.92) * mm, "end": v(5.04, 8.88) * mm});
            skLineSegment(sketch, "E475", {"start": v(5.04, 8.88) * mm, "end": v(5.3, 8.6) * mm});
            skLineSegment(sketch, "E476", {"start": v(5.3, 8.6) * mm, "end": v(5.73, 8.16) * mm});
            skLineSegment(sketch, "E477", {"start": v(5.73, 8.16) * mm, "end": v(6.19, 7.72) * mm});
            skLineSegment(sketch, "E478", {"start": v(6.19, 7.72) * mm, "end": v(6.49, 7.39) * mm});
            skLineSegment(sketch, "E479", {"start": v(6.49, 7.39) * mm, "end": v(6.45, 7.29) * mm});
            skLineSegment(sketch, "E480", {"start": v(6.45, 7.29) * mm, "end": v(6.04, 7.48) * mm});
            skLineSegment(sketch, "E481", {"start": v(6.04, 7.48) * mm, "end": v(5.91, 7.55) * mm});
            skLineSegment(sketch, "E482", {"start": v(5.91, 7.55) * mm, "end": v(5.54, 7.81) * mm});
            skLineSegment(sketch, "E483", {"start": v(5.54, 7.81) * mm, "end": v(4.45, 8.64) * mm});
            skLineSegment(sketch, "E484", {"start": v(4.45, 8.64) * mm, "end": v(3.59, 9.43) * mm});
            skLineSegment(sketch, "E485", {"start": v(3.59, 9.43) * mm, "end": v(3, 10.12) * mm});
            skLineSegment(sketch, "E486", {"start": v(3, 10.12) * mm, "end": v(2.56, 10.7) * mm});
            skLineSegment(sketch, "E487", {"start": v(2.56, 10.7) * mm, "end": v(2.41, 10.89) * mm});
            skLineSegment(sketch, "E488", {"start": v(1.92, -13.3) * mm, "end": v(1.96, -13.73) * mm});
            skCircle(sketch, "E489.cCircle", {"center": v(0, 0) * mm, "radius": 41.92 * mm, "construction": true});
            skLineSegment(sketch, "E489.0", {"start": v(24.2, -41.92) * mm, "end": v(-24.2, -41.92) * mm});
            skLineSegment(sketch, "E489.1", {"start": v(-24.2, -41.92) * mm, "end": v(-48.4, 0) * mm});
            skLineSegment(sketch, "E489.2", {"start": v(-48.4, 0) * mm, "end": v(-24.2, 41.92) * mm});
            skLineSegment(sketch, "E489.3", {"start": v(-24.2, 41.92) * mm, "end": v(24.2, 41.92) * mm});
            skLineSegment(sketch, "E489.4", {"start": v(24.2, 41.92) * mm, "end": v(48.4, 0) * mm});
            skLineSegment(sketch, "E489.5", {"start": v(48.4, 0) * mm, "end": v(24.2, -41.92) * mm});
            skPoint(sketch, "E489.0.midPoint", {"position": v(0, -41.92) * mm});
            skLineSegment(sketch, "E490", {"start": v(-3.18, 32.4) * mm, "end": v(-3.18, 37.16) * mm});
            skLineSegment(sketch, "E491", {"start": v(3.17, 32.4) * mm, "end": v(3.17, 37.16) * mm});
            skPoint(sketch, "E492.start.orphan", {"position": v(0, 41.92) * mm});
            skLineSegment(sketch, "E493", {"start": v(-3.18, 32.4) * mm, "end": v(3.17, 32.4) * mm});
            skLineSegment(sketch, "E494", {"start": v(28.06, -16.2) * mm, "end": v(29.64, -13.45) * mm});
            skLineSegment(sketch, "E495", {"start": v(29.64, -13.45) * mm, "end": v(33.77, -15.83) * mm});
            skLineSegment(sketch, "E496", {"start": v(28.06, -16.2) * mm, "end": v(26.47, -18.95) * mm});
            skLineSegment(sketch, "E497", {"start": v(26.47, -18.95) * mm, "end": v(30.6, -21.33) * mm});
            skPoint(sketch, "E498.start.orphan", {"position": v(36.3, -20.96) * mm});
            skLineSegment(sketch, "E499", {"start": v(-28.06, -16.2) * mm, "end": v(-26.47, -18.95) * mm});
            skLineSegment(sketch, "E500", {"start": v(-26.47, -18.95) * mm, "end": v(-30.6, -21.33) * mm});
            skLineSegment(sketch, "E501", {"start": v(-28.06, -16.2) * mm, "end": v(-29.64, -13.45) * mm});
            skLineSegment(sketch, "E502", {"start": v(-29.64, -13.45) * mm, "end": v(-33.77, -15.83) * mm});
            skPoint(sketch, "E503.start.orphan", {"position": v(-36.3, -20.96) * mm});
            skLineSegment(sketch, "E504.bottom", {"start": v(3.85, 22.19) * mm, "end": v(-3.85, 22.19) * mm});
            skLineSegment(sketch, "E504.top", {"start": v(3.85, 29.88) * mm, "end": v(-3.85, 29.88) * mm});
            skLineSegment(sketch, "E504.left", {"start": v(3.85, 22.19) * mm, "end": v(3.85, 29.88) * mm});
            skLineSegment(sketch, "E504.right", {"start": v(-3.85, 22.19) * mm, "end": v(-3.85, 29.88) * mm});
            skPoint(sketch, "E504.middle", {"position": v(0, 26.04) * mm});
            skLineSegment(sketch, "E505.bottom", {"start": v(3.85, -29.88) * mm, "end": v(-3.85, -29.88) * mm});
            skLineSegment(sketch, "E505.top", {"start": v(3.85, -22.19) * mm, "end": v(-3.85, -22.19) * mm});
            skLineSegment(sketch, "E505.left", {"start": v(3.85, -29.88) * mm, "end": v(3.85, -22.19) * mm});
            skLineSegment(sketch, "E505.right", {"start": v(-3.85, -29.88) * mm, "end": v(-3.85, -22.19) * mm});
            skPoint(sketch, "E505.middle", {"position": v(0, -26.04) * mm});
            skLineSegment(sketch, "E506", {"start": v(-17.16, 25.87) * mm, "end": v(-16.43, 25.66) * mm});
            skLineSegment(sketch, "E507", {"start": v(30.6, -21.33) * mm, "end": v(31.23, -20.23) * mm});
            skLineSegment(sketch, "E508", {"start": v(31.23, -20.23) * mm, "end": v(35.35, -22.61) * mm});
            skLineSegment(sketch, "E509", {"start": v(33.77, -15.83) * mm, "end": v(33.13, -16.93) * mm});
            skLineSegment(sketch, "E510", {"start": v(33.13, -16.93) * mm, "end": v(37.26, -19.31) * mm});
            skLineSegment(sketch, "E511.trimOffspring", {"start": v(34.61, -23.65) * mm, "end": v(34.72, -23.71) * mm});
            skLineSegment(sketch, "E512.trimOffspring", {"start": v(37.79, -18.15) * mm, "end": v(37.9, -18.21) * mm});
            skLineSegment(sketch, "E513", {"start": v(-30.6, -21.33) * mm, "end": v(-31.23, -20.23) * mm});
            skLineSegment(sketch, "E514", {"start": v(-31.23, -20.23) * mm, "end": v(-35.35, -22.61) * mm});
            skLineSegment(sketch, "E515.trimOffspring", {"start": v(-34.61, -23.65) * mm, "end": v(-34.72, -23.71) * mm});
            skLineSegment(sketch, "E516", {"start": v(-33.77, -15.83) * mm, "end": v(-33.13, -16.93) * mm});
            skLineSegment(sketch, "E517", {"start": v(-33.13, -16.93) * mm, "end": v(-37.26, -19.31) * mm});
            skLineSegment(sketch, "E518.trimOffspring", {"start": v(-37.79, -18.15) * mm, "end": v(-37.9, -18.21) * mm});
            skLineSegment(sketch, "E519", {"start": v(3.17, 37.16) * mm, "end": v(1.9, 37.16) * mm});
            skLineSegment(sketch, "E520", {"start": v(1.9, 37.16) * mm, "end": v(1.9, 41.92) * mm});
            skLineSegment(sketch, "E521", {"start": v(-3.18, 37.16) * mm, "end": v(-1.9, 37.16) * mm});
            skLineSegment(sketch, "E522", {"start": v(-1.9, 37.16) * mm, "end": v(-1.9, 41.92) * mm});
            skLineSegment(sketch, "E523.trimOffspring", {"start": v(3.17, 41.8) * mm, "end": v(3.17, 41.92) * mm});
            skLineSegment(sketch, "E524.trimOffspring", {"start": v(-3.18, 41.8) * mm, "end": v(-3.18, 41.92) * mm});
            skSolve(sketch);
        }
        {
            var Q0;
            Q0=makeQuery(id+"F0.imprint","IMPRINT",FACE,{"disambiguationData":[TD([[makeQuery(id+"F0.imprint","IMPRINT",EDGE,{"derivedFrom":sQuery(id+"F0.wireOp",EDGE,"E0")}),1.0]])]});
            extrude(context, id + "F1", {"entities" : qUnion([Q0]), "depth" : 10.16 * mm, "offsetDistance" : 25.4 * mm});
        }
        {
            var Q0;
            Q0=makeQuery(id+"F0.imprint","IMPRINT",FACE,{"disambiguationData":[TD([[makeQuery(id+"F0.imprint","IMPRINT",EDGE,{"derivedFrom":sQuery(id+"F0.wireOp",EDGE,"E0")}),-1.0]])]});
            var Q1;
            Q1=makeQuery(id+"F0.imprint","IMPRINT",FACE,{"disambiguationData":[TD([[makeQuery(id+"F0.imprint","IMPRINT",EDGE,{"derivedFrom":sQuery(id+"F0.wireOp",EDGE,"E369")}),-1.0]])]});
            var Q2;
            Q2=makeQuery(id+"F0.imprint","IMPRINT",FACE,{"disambiguationData":[TD([[makeQuery(id+"F0.imprint","IMPRINT",EDGE,{"derivedFrom":sQuery(id+"F0.wireOp",EDGE,"E301")}),-1.0]])]});
            var Q3;
            Q3=makeQuery(id+"F0.imprint","IMPRINT",FACE,{"disambiguationData":[TD([[makeQuery(id+"F0.imprint","IMPRINT",EDGE,{"derivedFrom":sQuery(id+"F0.wireOp",EDGE,"E167")}),-1.0]])]});
            var Q4;
            Q4=makeQuery(id+"F0.imprint","IMPRINT",FACE,{"disambiguationData":[TD([[makeQuery(id+"F0.imprint","IMPRINT",EDGE,{"derivedFrom":sQuery(id+"F0.wireOp",EDGE,"E249")}),-1.0]])]});
            var Q5;
            Q5=makeQuery(id+"F0.imprint","IMPRINT",FACE,{"disambiguationData":[TD([[makeQuery(id+"F0.imprint","IMPRINT",EDGE,{"derivedFrom":sQuery(id+"F0.wireOp",EDGE,"E95")}),-1.0]])]});
            var Q6;
            Q6=makeQuery(id+"F0.imprint","IMPRINT",FACE,{"disambiguationData":[TD([[makeQuery(id+"F0.imprint","IMPRINT",EDGE,{"derivedFrom":sQuery(id+"F0.wireOp",EDGE,"E73")}),-1.0]])]});
            extrude(context, id + "F2", {"entities" : qUnion([Q0, Q1, Q2, Q3, Q4, Q5, Q6]), "operationType" : NewBodyOperationType.ADD, "depth" : 9.4 * mm, "offsetDistance" : 25.4 * mm});
        }
        {
            var Q0;
            Q0=makeQuery(id+"F0.imprint","IMPRINT",FACE,{"disambiguationData":[TD([[makeQuery(id+"F0.imprint","IMPRINT",EDGE,{"derivedFrom":sQuery(id+"F0.wireOp",EDGE,"E494")}),-1.0]])]});
            var Q1;
            Q1=makeQuery(id+"F0.imprint","IMPRINT",FACE,{"disambiguationData":[TD([[makeQuery(id+"F0.imprint","IMPRINT",EDGE,{"derivedFrom":sQuery(id+"F0.wireOp",EDGE,"E499")}),-1.0]])]});
            var Q2;
            Q2=makeQuery(id+"F0.imprint","IMPRINT",FACE,{"disambiguationData":[TD([[makeQuery(id+"F0.imprint","IMPRINT",EDGE,{"derivedFrom":sQuery(id+"F0.wireOp",EDGE,"E490")}),-1.0]])]});
            extrude(context, id + "F3", {"entities" : qUnion([Q0, Q1, Q2]), "operationType" : NewBodyOperationType.ADD, "depth" : 3.17 * mm, "offsetDistance" : 25.4 * mm});
        }
        {
            var Q0;
            Q0=makeQuery(id+"F1.opExtrude","SWEPT_BODY",BODY,{"disambiguationData":[OSD([sQuery(id+"F0.wireOp",EDGE,"E0"),sQuery(id+"F0.wireOp",EDGE,"E1"),sQuery(id+"F0.wireOp",EDGE,"E2"),sQuery(id+"F0.wireOp",EDGE,"E3"),sQuery(id+"F0.wireOp",EDGE,"E4"),sQuery(id+"F0.wireOp",EDGE,"E5"),sQuery(id+"F0.wireOp",EDGE,"E6"),sQuery(id+"F0.wireOp",EDGE,"E7"),sQuery(id+"F0.wireOp",EDGE,"E8"),sQuery(id+"F0.wireOp",EDGE,"E9"),sQuery(id+"F0.wireOp",EDGE,"E10"),sQuery(id+"F0.wireOp",EDGE,"E11"),sQuery(id+"F0.wireOp",EDGE,"E12"),sQuery(id+"F0.wireOp",EDGE,"E13"),sQuery(id+"F0.wireOp",EDGE,"E14"),sQuery(id+"F0.wireOp",EDGE,"E15"),sQuery(id+"F0.wireOp",EDGE,"E16"),sQuery(id+"F0.wireOp",EDGE,"E17"),sQuery(id+"F0.wireOp",EDGE,"E18"),sQuery(id+"F0.wireOp",EDGE,"E19"),sQuery(id+"F0.wireOp",EDGE,"E20"),sQuery(id+"F0.wireOp",EDGE,"E21"),sQuery(id+"F0.wireOp",EDGE,"E22"),sQuery(id+"F0.wireOp",EDGE,"E23"),sQuery(id+"F0.wireOp",EDGE,"E24"),sQuery(id+"F0.wireOp",EDGE,"E25"),sQuery(id+"F0.wireOp",EDGE,"E26"),sQuery(id+"F0.wireOp",EDGE,"E27"),sQuery(id+"F0.wireOp",EDGE,"E28"),sQuery(id+"F0.wireOp",EDGE,"E29"),sQuery(id+"F0.wireOp",EDGE,"E30"),sQuery(id+"F0.wireOp",EDGE,"E31"),sQuery(id+"F0.wireOp",EDGE,"E32"),sQuery(id+"F0.wireOp",EDGE,"E33"),sQuery(id+"F0.wireOp",EDGE,"E34"),sQuery(id+"F0.wireOp",EDGE,"E35"),sQuery(id+"F0.wireOp",EDGE,"E36"),sQuery(id+"F0.wireOp",EDGE,"E37"),sQuery(id+"F0.wireOp",EDGE,"E38"),sQuery(id+"F0.wireOp",EDGE,"E39"),sQuery(id+"F0.wireOp",EDGE,"E40"),sQuery(id+"F0.wireOp",EDGE,"E41"),sQuery(id+"F0.wireOp",EDGE,"E42"),sQuery(id+"F0.wireOp",EDGE,"E43"),sQuery(id+"F0.wireOp",EDGE,"E44"),sQuery(id+"F0.wireOp",EDGE,"E45"),sQuery(id+"F0.wireOp",EDGE,"E46"),sQuery(id+"F0.wireOp",EDGE,"E47"),sQuery(id+"F0.wireOp",EDGE,"E48"),sQuery(id+"F0.wireOp",EDGE,"E49"),sQuery(id+"F0.wireOp",EDGE,"E50"),sQuery(id+"F0.wireOp",EDGE,"E51"),sQuery(id+"F0.wireOp",EDGE,"E52"),sQuery(id+"F0.wireOp",EDGE,"E53"),sQuery(id+"F0.wireOp",EDGE,"E54"),sQuery(id+"F0.wireOp",EDGE,"E55"),sQuery(id+"F0.wireOp",EDGE,"E56"),sQuery(id+"F0.wireOp",EDGE,"E57"),sQuery(id+"F0.wireOp",EDGE,"E58"),sQuery(id+"F0.wireOp",EDGE,"E59"),sQuery(id+"F0.wireOp",EDGE,"E60"),sQuery(id+"F0.wireOp",EDGE,"E61"),sQuery(id+"F0.wireOp",EDGE,"E62"),sQuery(id+"F0.wireOp",EDGE,"E63"),sQuery(id+"F0.wireOp",EDGE,"E64"),sQuery(id+"F0.wireOp",EDGE,"E65"),sQuery(id+"F0.wireOp",EDGE,"E66"),sQuery(id+"F0.wireOp",EDGE,"E67"),sQuery(id+"F0.wireOp",EDGE,"E68"),sQuery(id+"F0.wireOp",EDGE,"E69"),sQuery(id+"F0.wireOp",EDGE,"E70"),sQuery(id+"F0.wireOp",EDGE,"E71"),sQuery(id+"F0.wireOp",EDGE,"E72"),sQuery(id+"F0.wireOp",EDGE,"E73"),sQuery(id+"F0.wireOp",EDGE,"E74"),sQuery(id+"F0.wireOp",EDGE,"E75"),sQuery(id+"F0.wireOp",EDGE,"E76"),sQuery(id+"F0.wireOp",EDGE,"E77"),sQuery(id+"F0.wireOp",EDGE,"E78"),sQuery(id+"F0.wireOp",EDGE,"E79"),sQuery(id+"F0.wireOp",EDGE,"E80"),sQuery(id+"F0.wireOp",EDGE,"E81"),sQuery(id+"F0.wireOp",EDGE,"E82"),sQuery(id+"F0.wireOp",EDGE,"E83"),sQuery(id+"F0.wireOp",EDGE,"E84"),sQuery(id+"F0.wireOp",EDGE,"E85"),sQuery(id+"F0.wireOp",EDGE,"E86"),sQuery(id+"F0.wireOp",EDGE,"E87"),sQuery(id+"F0.wireOp",EDGE,"E88"),sQuery(id+"F0.wireOp",EDGE,"E89"),sQuery(id+"F0.wireOp",EDGE,"E90"),sQuery(id+"F0.wireOp",EDGE,"E91"),sQuery(id+"F0.wireOp",EDGE,"E92"),sQuery(id+"F0.wireOp",EDGE,"E93"),sQuery(id+"F0.wireOp",EDGE,"E94"),sQuery(id+"F0.wireOp",EDGE,"E95"),sQuery(id+"F0.wireOp",EDGE,"E96"),sQuery(id+"F0.wireOp",EDGE,"E97"),sQuery(id+"F0.wireOp",EDGE,"E98"),sQuery(id+"F0.wireOp",EDGE,"E99"),sQuery(id+"F0.wireOp",EDGE,"E100"),sQuery(id+"F0.wireOp",EDGE,"E101"),sQuery(id+"F0.wireOp",EDGE,"E102"),sQuery(id+"F0.wireOp",EDGE,"E103"),sQuery(id+"F0.wireOp",EDGE,"E104"),sQuery(id+"F0.wireOp",EDGE,"E105"),sQuery(id+"F0.wireOp",EDGE,"E106"),sQuery(id+"F0.wireOp",EDGE,"E107"),sQuery(id+"F0.wireOp",EDGE,"E108"),sQuery(id+"F0.wireOp",EDGE,"E109"),sQuery(id+"F0.wireOp",EDGE,"E110"),sQuery(id+"F0.wireOp",EDGE,"E111"),sQuery(id+"F0.wireOp",EDGE,"E112"),sQuery(id+"F0.wireOp",EDGE,"E113"),sQuery(id+"F0.wireOp",EDGE,"E114"),sQuery(id+"F0.wireOp",EDGE,"E115"),sQuery(id+"F0.wireOp",EDGE,"E116"),sQuery(id+"F0.wireOp",EDGE,"E117"),sQuery(id+"F0.wireOp",EDGE,"E118"),sQuery(id+"F0.wireOp",EDGE,"E119"),sQuery(id+"F0.wireOp",EDGE,"E120"),sQuery(id+"F0.wireOp",EDGE,"E121"),sQuery(id+"F0.wireOp",EDGE,"E122"),sQuery(id+"F0.wireOp",EDGE,"E123"),sQuery(id+"F0.wireOp",EDGE,"E124"),sQuery(id+"F0.wireOp",EDGE,"E125"),sQuery(id+"F0.wireOp",EDGE,"E126"),sQuery(id+"F0.wireOp",EDGE,"E127"),sQuery(id+"F0.wireOp",EDGE,"E128"),sQuery(id+"F0.wireOp",EDGE,"E129"),sQuery(id+"F0.wireOp",EDGE,"E130"),sQuery(id+"F0.wireOp",EDGE,"E131"),sQuery(id+"F0.wireOp",EDGE,"E132"),sQuery(id+"F0.wireOp",EDGE,"E133"),sQuery(id+"F0.wireOp",EDGE,"E134"),sQuery(id+"F0.wireOp",EDGE,"E135"),sQuery(id+"F0.wireOp",EDGE,"E136"),sQuery(id+"F0.wireOp",EDGE,"E137"),sQuery(id+"F0.wireOp",EDGE,"E138"),sQuery(id+"F0.wireOp",EDGE,"E139"),sQuery(id+"F0.wireOp",EDGE,"E140"),sQuery(id+"F0.wireOp",EDGE,"E141"),sQuery(id+"F0.wireOp",EDGE,"E142"),sQuery(id+"F0.wireOp",EDGE,"E143"),sQuery(id+"F0.wireOp",EDGE,"E144"),sQuery(id+"F0.wireOp",EDGE,"E145"),sQuery(id+"F0.wireOp",EDGE,"E146"),sQuery(id+"F0.wireOp",EDGE,"E147"),sQuery(id+"F0.wireOp",EDGE,"E148"),sQuery(id+"F0.wireOp",EDGE,"E149"),sQuery(id+"F0.wireOp",EDGE,"E150"),sQuery(id+"F0.wireOp",EDGE,"E151"),sQuery(id+"F0.wireOp",EDGE,"E152"),sQuery(id+"F0.wireOp",EDGE,"E153"),sQuery(id+"F0.wireOp",EDGE,"E154"),sQuery(id+"F0.wireOp",EDGE,"E155"),sQuery(id+"F0.wireOp",EDGE,"E156"),sQuery(id+"F0.wireOp",EDGE,"E157"),sQuery(id+"F0.wireOp",EDGE,"E158"),sQuery(id+"F0.wireOp",EDGE,"E159"),sQuery(id+"F0.wireOp",EDGE,"E160"),sQuery(id+"F0.wireOp",EDGE,"E161"),sQuery(id+"F0.wireOp",EDGE,"E162"),sQuery(id+"F0.wireOp",EDGE,"E163"),sQuery(id+"F0.wireOp",EDGE,"E164"),sQuery(id+"F0.wireOp",EDGE,"E165"),sQuery(id+"F0.wireOp",EDGE,"E166"),sQuery(id+"F0.wireOp",EDGE,"E167"),sQuery(id+"F0.wireOp",EDGE,"E168"),sQuery(id+"F0.wireOp",EDGE,"E169"),sQuery(id+"F0.wireOp",EDGE,"E170"),sQuery(id+"F0.wireOp",EDGE,"E171"),sQuery(id+"F0.wireOp",EDGE,"E172"),sQuery(id+"F0.wireOp",EDGE,"E173"),sQuery(id+"F0.wireOp",EDGE,"E174"),sQuery(id+"F0.wireOp",EDGE,"E175"),sQuery(id+"F0.wireOp",EDGE,"E176"),sQuery(id+"F0.wireOp",EDGE,"E177"),sQuery(id+"F0.wireOp",EDGE,"E178"),sQuery(id+"F0.wireOp",EDGE,"E179"),sQuery(id+"F0.wireOp",EDGE,"E180"),sQuery(id+"F0.wireOp",EDGE,"E181"),sQuery(id+"F0.wireOp",EDGE,"E182"),sQuery(id+"F0.wireOp",EDGE,"E183"),sQuery(id+"F0.wireOp",EDGE,"E184"),sQuery(id+"F0.wireOp",EDGE,"E185"),sQuery(id+"F0.wireOp",EDGE,"E186"),sQuery(id+"F0.wireOp",EDGE,"E187"),sQuery(id+"F0.wireOp",EDGE,"E188"),sQuery(id+"F0.wireOp",EDGE,"E189"),sQuery(id+"F0.wireOp",EDGE,"E190"),sQuery(id+"F0.wireOp",EDGE,"E191"),sQuery(id+"F0.wireOp",EDGE,"E192"),sQuery(id+"F0.wireOp",EDGE,"E193"),sQuery(id+"F0.wireOp",EDGE,"E194"),sQuery(id+"F0.wireOp",EDGE,"E195"),sQuery(id+"F0.wireOp",EDGE,"E196"),sQuery(id+"F0.wireOp",EDGE,"E197"),sQuery(id+"F0.wireOp",EDGE,"E198"),sQuery(id+"F0.wireOp",EDGE,"E199"),sQuery(id+"F0.wireOp",EDGE,"E200"),sQuery(id+"F0.wireOp",EDGE,"E201"),sQuery(id+"F0.wireOp",EDGE,"E202"),sQuery(id+"F0.wireOp",EDGE,"E203"),sQuery(id+"F0.wireOp",EDGE,"E204"),sQuery(id+"F0.wireOp",EDGE,"E205"),sQuery(id+"F0.wireOp",EDGE,"E206"),sQuery(id+"F0.wireOp",EDGE,"E207"),sQuery(id+"F0.wireOp",EDGE,"E208"),sQuery(id+"F0.wireOp",EDGE,"E209"),sQuery(id+"F0.wireOp",EDGE,"E210"),sQuery(id+"F0.wireOp",EDGE,"E211"),sQuery(id+"F0.wireOp",EDGE,"E212"),sQuery(id+"F0.wireOp",EDGE,"E213"),sQuery(id+"F0.wireOp",EDGE,"E214"),sQuery(id+"F0.wireOp",EDGE,"E215"),sQuery(id+"F0.wireOp",EDGE,"E216"),sQuery(id+"F0.wireOp",EDGE,"E217"),sQuery(id+"F0.wireOp",EDGE,"E218"),sQuery(id+"F0.wireOp",EDGE,"E219"),sQuery(id+"F0.wireOp",EDGE,"E220"),sQuery(id+"F0.wireOp",EDGE,"E221"),sQuery(id+"F0.wireOp",EDGE,"E222"),sQuery(id+"F0.wireOp",EDGE,"E223"),sQuery(id+"F0.wireOp",EDGE,"E224"),sQuery(id+"F0.wireOp",EDGE,"E225"),sQuery(id+"F0.wireOp",EDGE,"E226"),sQuery(id+"F0.wireOp",EDGE,"E227"),sQuery(id+"F0.wireOp",EDGE,"E228"),sQuery(id+"F0.wireOp",EDGE,"E229"),sQuery(id+"F0.wireOp",EDGE,"E230"),sQuery(id+"F0.wireOp",EDGE,"E231"),sQuery(id+"F0.wireOp",EDGE,"E232"),sQuery(id+"F0.wireOp",EDGE,"E233"),sQuery(id+"F0.wireOp",EDGE,"E234"),sQuery(id+"F0.wireOp",EDGE,"E235"),sQuery(id+"F0.wireOp",EDGE,"E236"),sQuery(id+"F0.wireOp",EDGE,"E237"),sQuery(id+"F0.wireOp",EDGE,"E238"),sQuery(id+"F0.wireOp",EDGE,"E239"),sQuery(id+"F0.wireOp",EDGE,"E240"),sQuery(id+"F0.wireOp",EDGE,"E241"),sQuery(id+"F0.wireOp",EDGE,"E242"),sQuery(id+"F0.wireOp",EDGE,"E243"),sQuery(id+"F0.wireOp",EDGE,"E244"),sQuery(id+"F0.wireOp",EDGE,"E245"),sQuery(id+"F0.wireOp",EDGE,"E246"),sQuery(id+"F0.wireOp",EDGE,"E247"),sQuery(id+"F0.wireOp",EDGE,"E248"),sQuery(id+"F0.wireOp",EDGE,"E249"),sQuery(id+"F0.wireOp",EDGE,"E250"),sQuery(id+"F0.wireOp",EDGE,"E251"),sQuery(id+"F0.wireOp",EDGE,"E252"),sQuery(id+"F0.wireOp",EDGE,"E253"),sQuery(id+"F0.wireOp",EDGE,"E254"),sQuery(id+"F0.wireOp",EDGE,"E255"),sQuery(id+"F0.wireOp",EDGE,"E256"),sQuery(id+"F0.wireOp",EDGE,"E257"),sQuery(id+"F0.wireOp",EDGE,"E258"),sQuery(id+"F0.wireOp",EDGE,"E259"),sQuery(id+"F0.wireOp",EDGE,"E260"),sQuery(id+"F0.wireOp",EDGE,"E261"),sQuery(id+"F0.wireOp",EDGE,"E262"),sQuery(id+"F0.wireOp",EDGE,"E263"),sQuery(id+"F0.wireOp",EDGE,"E264"),sQuery(id+"F0.wireOp",EDGE,"E265"),sQuery(id+"F0.wireOp",EDGE,"E266"),sQuery(id+"F0.wireOp",EDGE,"E267"),sQuery(id+"F0.wireOp",EDGE,"E268"),sQuery(id+"F0.wireOp",EDGE,"E269"),sQuery(id+"F0.wireOp",EDGE,"E270"),sQuery(id+"F0.wireOp",EDGE,"E271"),sQuery(id+"F0.wireOp",EDGE,"E272"),sQuery(id+"F0.wireOp",EDGE,"E273"),sQuery(id+"F0.wireOp",EDGE,"E274"),sQuery(id+"F0.wireOp",EDGE,"E275"),sQuery(id+"F0.wireOp",EDGE,"E276"),sQuery(id+"F0.wireOp",EDGE,"E277"),sQuery(id+"F0.wireOp",EDGE,"E278"),sQuery(id+"F0.wireOp",EDGE,"E279"),sQuery(id+"F0.wireOp",EDGE,"E280"),sQuery(id+"F0.wireOp",EDGE,"E281"),sQuery(id+"F0.wireOp",EDGE,"E282"),sQuery(id+"F0.wireOp",EDGE,"E283"),sQuery(id+"F0.wireOp",EDGE,"E284"),sQuery(id+"F0.wireOp",EDGE,"E285"),sQuery(id+"F0.wireOp",EDGE,"E286"),sQuery(id+"F0.wireOp",EDGE,"E287"),sQuery(id+"F0.wireOp",EDGE,"E288"),sQuery(id+"F0.wireOp",EDGE,"E289"),sQuery(id+"F0.wireOp",EDGE,"E290"),sQuery(id+"F0.wireOp",EDGE,"E291"),sQuery(id+"F0.wireOp",EDGE,"E292"),sQuery(id+"F0.wireOp",EDGE,"E293"),sQuery(id+"F0.wireOp",EDGE,"E294"),sQuery(id+"F0.wireOp",EDGE,"E295"),sQuery(id+"F0.wireOp",EDGE,"E296"),sQuery(id+"F0.wireOp",EDGE,"E297"),sQuery(id+"F0.wireOp",EDGE,"E298"),sQuery(id+"F0.wireOp",EDGE,"E299"),sQuery(id+"F0.wireOp",EDGE,"E300"),sQuery(id+"F0.wireOp",EDGE,"E301"),sQuery(id+"F0.wireOp",EDGE,"E302"),sQuery(id+"F0.wireOp",EDGE,"E303"),sQuery(id+"F0.wireOp",EDGE,"E304"),sQuery(id+"F0.wireOp",EDGE,"E305"),sQuery(id+"F0.wireOp",EDGE,"E306"),sQuery(id+"F0.wireOp",EDGE,"E307"),sQuery(id+"F0.wireOp",EDGE,"E308"),sQuery(id+"F0.wireOp",EDGE,"E309"),sQuery(id+"F0.wireOp",EDGE,"E310"),sQuery(id+"F0.wireOp",EDGE,"E311"),sQuery(id+"F0.wireOp",EDGE,"E312"),sQuery(id+"F0.wireOp",EDGE,"E313"),sQuery(id+"F0.wireOp",EDGE,"E314"),sQuery(id+"F0.wireOp",EDGE,"E315"),sQuery(id+"F0.wireOp",EDGE,"E316"),sQuery(id+"F0.wireOp",EDGE,"E317"),sQuery(id+"F0.wireOp",EDGE,"E318"),sQuery(id+"F0.wireOp",EDGE,"E319"),sQuery(id+"F0.wireOp",EDGE,"E320"),sQuery(id+"F0.wireOp",EDGE,"E321"),sQuery(id+"F0.wireOp",EDGE,"E322"),sQuery(id+"F0.wireOp",EDGE,"E323"),sQuery(id+"F0.wireOp",EDGE,"E324"),sQuery(id+"F0.wireOp",EDGE,"E325"),sQuery(id+"F0.wireOp",EDGE,"E326"),sQuery(id+"F0.wireOp",EDGE,"E327"),sQuery(id+"F0.wireOp",EDGE,"E328"),sQuery(id+"F0.wireOp",EDGE,"E329"),sQuery(id+"F0.wireOp",EDGE,"E330"),sQuery(id+"F0.wireOp",EDGE,"E331"),sQuery(id+"F0.wireOp",EDGE,"E332"),sQuery(id+"F0.wireOp",EDGE,"E333"),sQuery(id+"F0.wireOp",EDGE,"E334"),sQuery(id+"F0.wireOp",EDGE,"E335"),sQuery(id+"F0.wireOp",EDGE,"E336"),sQuery(id+"F0.wireOp",EDGE,"E337"),sQuery(id+"F0.wireOp",EDGE,"E338"),sQuery(id+"F0.wireOp",EDGE,"E339"),sQuery(id+"F0.wireOp",EDGE,"E340"),sQuery(id+"F0.wireOp",EDGE,"E341"),sQuery(id+"F0.wireOp",EDGE,"E342"),sQuery(id+"F0.wireOp",EDGE,"E343"),sQuery(id+"F0.wireOp",EDGE,"E344"),sQuery(id+"F0.wireOp",EDGE,"E345"),sQuery(id+"F0.wireOp",EDGE,"E346"),sQuery(id+"F0.wireOp",EDGE,"E347"),sQuery(id+"F0.wireOp",EDGE,"E348"),sQuery(id+"F0.wireOp",EDGE,"E349"),sQuery(id+"F0.wireOp",EDGE,"E350"),sQuery(id+"F0.wireOp",EDGE,"E351"),sQuery(id+"F0.wireOp",EDGE,"E352"),sQuery(id+"F0.wireOp",EDGE,"E353"),sQuery(id+"F0.wireOp",EDGE,"E354"),sQuery(id+"F0.wireOp",EDGE,"E355"),sQuery(id+"F0.wireOp",EDGE,"E356"),sQuery(id+"F0.wireOp",EDGE,"E357"),sQuery(id+"F0.wireOp",EDGE,"E358"),sQuery(id+"F0.wireOp",EDGE,"E359"),sQuery(id+"F0.wireOp",EDGE,"E360"),sQuery(id+"F0.wireOp",EDGE,"E361"),sQuery(id+"F0.wireOp",EDGE,"E362"),sQuery(id+"F0.wireOp",EDGE,"E363"),sQuery(id+"F0.wireOp",EDGE,"E364"),sQuery(id+"F0.wireOp",EDGE,"E365"),sQuery(id+"F0.wireOp",EDGE,"E366"),sQuery(id+"F0.wireOp",EDGE,"E367"),sQuery(id+"F0.wireOp",EDGE,"E368"),sQuery(id+"F0.wireOp",EDGE,"E369"),sQuery(id+"F0.wireOp",EDGE,"E370"),sQuery(id+"F0.wireOp",EDGE,"E371"),sQuery(id+"F0.wireOp",EDGE,"E372"),sQuery(id+"F0.wireOp",EDGE,"E373"),sQuery(id+"F0.wireOp",EDGE,"E374"),sQuery(id+"F0.wireOp",EDGE,"E375"),sQuery(id+"F0.wireOp",EDGE,"E376"),sQuery(id+"F0.wireOp",EDGE,"E377"),sQuery(id+"F0.wireOp",EDGE,"E378"),sQuery(id+"F0.wireOp",EDGE,"E379"),sQuery(id+"F0.wireOp",EDGE,"E380"),sQuery(id+"F0.wireOp",EDGE,"E381"),sQuery(id+"F0.wireOp",EDGE,"E382"),sQuery(id+"F0.wireOp",EDGE,"E383"),sQuery(id+"F0.wireOp",EDGE,"E384"),sQuery(id+"F0.wireOp",EDGE,"E385"),sQuery(id+"F0.wireOp",EDGE,"E386"),sQuery(id+"F0.wireOp",EDGE,"E387"),sQuery(id+"F0.wireOp",EDGE,"E388"),sQuery(id+"F0.wireOp",EDGE,"E389"),sQuery(id+"F0.wireOp",EDGE,"E390"),sQuery(id+"F0.wireOp",EDGE,"E391"),sQuery(id+"F0.wireOp",EDGE,"E392"),sQuery(id+"F0.wireOp",EDGE,"E393"),sQuery(id+"F0.wireOp",EDGE,"E394"),sQuery(id+"F0.wireOp",EDGE,"E395"),sQuery(id+"F0.wireOp",EDGE,"E396"),sQuery(id+"F0.wireOp",EDGE,"E397"),sQuery(id+"F0.wireOp",EDGE,"E398"),sQuery(id+"F0.wireOp",EDGE,"E399"),sQuery(id+"F0.wireOp",EDGE,"E400"),sQuery(id+"F0.wireOp",EDGE,"E401"),sQuery(id+"F0.wireOp",EDGE,"E402"),sQuery(id+"F0.wireOp",EDGE,"E403"),sQuery(id+"F0.wireOp",EDGE,"E404"),sQuery(id+"F0.wireOp",EDGE,"E405"),sQuery(id+"F0.wireOp",EDGE,"E406"),sQuery(id+"F0.wireOp",EDGE,"E407"),sQuery(id+"F0.wireOp",EDGE,"E408"),sQuery(id+"F0.wireOp",EDGE,"E409"),sQuery(id+"F0.wireOp",EDGE,"E410"),sQuery(id+"F0.wireOp",EDGE,"E411"),sQuery(id+"F0.wireOp",EDGE,"E412"),sQuery(id+"F0.wireOp",EDGE,"E413"),sQuery(id+"F0.wireOp",EDGE,"E414"),sQuery(id+"F0.wireOp",EDGE,"E415"),sQuery(id+"F0.wireOp",EDGE,"E416"),sQuery(id+"F0.wireOp",EDGE,"E417"),sQuery(id+"F0.wireOp",EDGE,"E418"),sQuery(id+"F0.wireOp",EDGE,"E419"),sQuery(id+"F0.wireOp",EDGE,"E420"),sQuery(id+"F0.wireOp",EDGE,"E421"),sQuery(id+"F0.wireOp",EDGE,"E422"),sQuery(id+"F0.wireOp",EDGE,"E423"),sQuery(id+"F0.wireOp",EDGE,"E424"),sQuery(id+"F0.wireOp",EDGE,"E425"),sQuery(id+"F0.wireOp",EDGE,"E426"),sQuery(id+"F0.wireOp",EDGE,"E427"),sQuery(id+"F0.wireOp",EDGE,"E428"),sQuery(id+"F0.wireOp",EDGE,"E429"),sQuery(id+"F0.wireOp",EDGE,"E430"),sQuery(id+"F0.wireOp",EDGE,"E431"),sQuery(id+"F0.wireOp",EDGE,"E432"),sQuery(id+"F0.wireOp",EDGE,"E433"),sQuery(id+"F0.wireOp",EDGE,"E434"),sQuery(id+"F0.wireOp",EDGE,"E435"),sQuery(id+"F0.wireOp",EDGE,"E436"),sQuery(id+"F0.wireOp",EDGE,"E437"),sQuery(id+"F0.wireOp",EDGE,"E438"),sQuery(id+"F0.wireOp",EDGE,"E439"),sQuery(id+"F0.wireOp",EDGE,"E440"),sQuery(id+"F0.wireOp",EDGE,"E441"),sQuery(id+"F0.wireOp",EDGE,"E442"),sQuery(id+"F0.wireOp",EDGE,"E443"),sQuery(id+"F0.wireOp",EDGE,"E444"),sQuery(id+"F0.wireOp",EDGE,"E445"),sQuery(id+"F0.wireOp",EDGE,"E446"),sQuery(id+"F0.wireOp",EDGE,"E447"),sQuery(id+"F0.wireOp",EDGE,"E448"),sQuery(id+"F0.wireOp",EDGE,"E449"),sQuery(id+"F0.wireOp",EDGE,"E450"),sQuery(id+"F0.wireOp",EDGE,"E451"),sQuery(id+"F0.wireOp",EDGE,"E452"),sQuery(id+"F0.wireOp",EDGE,"E453"),sQuery(id+"F0.wireOp",EDGE,"E454"),sQuery(id+"F0.wireOp",EDGE,"E455"),sQuery(id+"F0.wireOp",EDGE,"E456"),sQuery(id+"F0.wireOp",EDGE,"E457"),sQuery(id+"F0.wireOp",EDGE,"E458"),sQuery(id+"F0.wireOp",EDGE,"E459"),sQuery(id+"F0.wireOp",EDGE,"E460"),sQuery(id+"F0.wireOp",EDGE,"E461"),sQuery(id+"F0.wireOp",EDGE,"E462"),sQuery(id+"F0.wireOp",EDGE,"E463"),sQuery(id+"F0.wireOp",EDGE,"E464"),sQuery(id+"F0.wireOp",EDGE,"E465"),sQuery(id+"F0.wireOp",EDGE,"E466"),sQuery(id+"F0.wireOp",EDGE,"E467"),sQuery(id+"F0.wireOp",EDGE,"E468"),sQuery(id+"F0.wireOp",EDGE,"E469"),sQuery(id+"F0.wireOp",EDGE,"E470"),sQuery(id+"F0.wireOp",EDGE,"E471"),sQuery(id+"F0.wireOp",EDGE,"E472"),sQuery(id+"F0.wireOp",EDGE,"E473"),sQuery(id+"F0.wireOp",EDGE,"E474"),sQuery(id+"F0.wireOp",EDGE,"E475"),sQuery(id+"F0.wireOp",EDGE,"E476"),sQuery(id+"F0.wireOp",EDGE,"E477"),sQuery(id+"F0.wireOp",EDGE,"E478"),sQuery(id+"F0.wireOp",EDGE,"E479"),sQuery(id+"F0.wireOp",EDGE,"E480"),sQuery(id+"F0.wireOp",EDGE,"E481"),sQuery(id+"F0.wireOp",EDGE,"E482"),sQuery(id+"F0.wireOp",EDGE,"E483"),sQuery(id+"F0.wireOp",EDGE,"E484"),sQuery(id+"F0.wireOp",EDGE,"E485"),sQuery(id+"F0.wireOp",EDGE,"E486"),sQuery(id+"F0.wireOp",EDGE,"E487"),sQuery(id+"F0.wireOp",EDGE,"E488"),sQuery(id+"F0.wireOp",EDGE,"E489.0"),sQuery(id+"F0.wireOp",EDGE,"E489.1"),sQuery(id+"F0.wireOp",EDGE,"E489.2"),sQuery(id+"F0.wireOp",EDGE,"E489.3"),sQuery(id+"F0.wireOp",EDGE,"E489.4"),sQuery(id+"F0.wireOp",EDGE,"E489.5"),sQuery(id+"F0.wireOp",EDGE,"E490"),sQuery(id+"F0.wireOp",EDGE,"E491"),sQuery(id+"F0.wireOp",EDGE,"E493"),sQuery(id+"F0.wireOp",EDGE,"E494"),sQuery(id+"F0.wireOp",EDGE,"E495"),sQuery(id+"F0.wireOp",EDGE,"E496"),sQuery(id+"F0.wireOp",EDGE,"E497"),sQuery(id+"F0.wireOp",EDGE,"E499"),sQuery(id+"F0.wireOp",EDGE,"E500"),sQuery(id+"F0.wireOp",EDGE,"E501"),sQuery(id+"F0.wireOp",EDGE,"E502"),sQuery(id+"F0.wireOp",EDGE,"E504.bottom"),sQuery(id+"F0.wireOp",EDGE,"E504.top"),sQuery(id+"F0.wireOp",EDGE,"E504.left"),sQuery(id+"F0.wireOp",EDGE,"E504.right"),sQuery(id+"F0.wireOp",EDGE,"E505.bottom"),sQuery(id+"F0.wireOp",EDGE,"E505.top"),sQuery(id+"F0.wireOp",EDGE,"E505.left"),sQuery(id+"F0.wireOp",EDGE,"E505.right"),sQuery(id+"F0.wireOp",EDGE,"E506"),sQuery(id+"F0.wireOp",EDGE,"E507"),sQuery(id+"F0.wireOp",EDGE,"E508"),sQuery(id+"F0.wireOp",EDGE,"E509"),sQuery(id+"F0.wireOp",EDGE,"E510"),sQuery(id+"F0.wireOp",EDGE,"E513"),sQuery(id+"F0.wireOp",EDGE,"E514"),sQuery(id+"F0.wireOp",EDGE,"E516"),sQuery(id+"F0.wireOp",EDGE,"E517"),sQuery(id+"F0.wireOp",EDGE,"E519"),sQuery(id+"F0.wireOp",EDGE,"E520"),sQuery(id+"F0.wireOp",EDGE,"E521"),sQuery(id+"F0.wireOp",EDGE,"E522")])]});
            var Q1;
            Q1=makeQuery(id+"F1.opExtrude","CAP_EDGE",EDGE,{"disambiguationData":[OSD([sQuery(id+"F0.wireOp",EDGE,"E490")])],"isStart":false});
            transform(context, id + "F4", {"entities" : qUnion([Q0]), "transformType" : TransformType.ROTATION, "transformAxis" : qUnion([Q1]), "angle" : 180 * degree, "makeCopy" : false});
        }
        {
            var Q0;
            Q0=makeQuery(id+"F1.opExtrude","SWEPT_BODY",BODY,{"disambiguationData":[OSD([sQuery(id+"F0.wireOp",EDGE,"E0"),sQuery(id+"F0.wireOp",EDGE,"E1"),sQuery(id+"F0.wireOp",EDGE,"E2"),sQuery(id+"F0.wireOp",EDGE,"E3"),sQuery(id+"F0.wireOp",EDGE,"E4"),sQuery(id+"F0.wireOp",EDGE,"E5"),sQuery(id+"F0.wireOp",EDGE,"E6"),sQuery(id+"F0.wireOp",EDGE,"E7"),sQuery(id+"F0.wireOp",EDGE,"E8"),sQuery(id+"F0.wireOp",EDGE,"E9"),sQuery(id+"F0.wireOp",EDGE,"E10"),sQuery(id+"F0.wireOp",EDGE,"E11"),sQuery(id+"F0.wireOp",EDGE,"E12"),sQuery(id+"F0.wireOp",EDGE,"E13"),sQuery(id+"F0.wireOp",EDGE,"E14"),sQuery(id+"F0.wireOp",EDGE,"E15"),sQuery(id+"F0.wireOp",EDGE,"E16"),sQuery(id+"F0.wireOp",EDGE,"E17"),sQuery(id+"F0.wireOp",EDGE,"E18"),sQuery(id+"F0.wireOp",EDGE,"E19"),sQuery(id+"F0.wireOp",EDGE,"E20"),sQuery(id+"F0.wireOp",EDGE,"E21"),sQuery(id+"F0.wireOp",EDGE,"E22"),sQuery(id+"F0.wireOp",EDGE,"E23"),sQuery(id+"F0.wireOp",EDGE,"E24"),sQuery(id+"F0.wireOp",EDGE,"E25"),sQuery(id+"F0.wireOp",EDGE,"E26"),sQuery(id+"F0.wireOp",EDGE,"E27"),sQuery(id+"F0.wireOp",EDGE,"E28"),sQuery(id+"F0.wireOp",EDGE,"E29"),sQuery(id+"F0.wireOp",EDGE,"E30"),sQuery(id+"F0.wireOp",EDGE,"E31"),sQuery(id+"F0.wireOp",EDGE,"E32"),sQuery(id+"F0.wireOp",EDGE,"E33"),sQuery(id+"F0.wireOp",EDGE,"E34"),sQuery(id+"F0.wireOp",EDGE,"E35"),sQuery(id+"F0.wireOp",EDGE,"E36"),sQuery(id+"F0.wireOp",EDGE,"E37"),sQuery(id+"F0.wireOp",EDGE,"E38"),sQuery(id+"F0.wireOp",EDGE,"E39"),sQuery(id+"F0.wireOp",EDGE,"E40"),sQuery(id+"F0.wireOp",EDGE,"E41"),sQuery(id+"F0.wireOp",EDGE,"E42"),sQuery(id+"F0.wireOp",EDGE,"E43"),sQuery(id+"F0.wireOp",EDGE,"E44"),sQuery(id+"F0.wireOp",EDGE,"E45"),sQuery(id+"F0.wireOp",EDGE,"E46"),sQuery(id+"F0.wireOp",EDGE,"E47"),sQuery(id+"F0.wireOp",EDGE,"E48"),sQuery(id+"F0.wireOp",EDGE,"E49"),sQuery(id+"F0.wireOp",EDGE,"E50"),sQuery(id+"F0.wireOp",EDGE,"E51"),sQuery(id+"F0.wireOp",EDGE,"E52"),sQuery(id+"F0.wireOp",EDGE,"E53"),sQuery(id+"F0.wireOp",EDGE,"E54"),sQuery(id+"F0.wireOp",EDGE,"E55"),sQuery(id+"F0.wireOp",EDGE,"E56"),sQuery(id+"F0.wireOp",EDGE,"E57"),sQuery(id+"F0.wireOp",EDGE,"E58"),sQuery(id+"F0.wireOp",EDGE,"E59"),sQuery(id+"F0.wireOp",EDGE,"E60"),sQuery(id+"F0.wireOp",EDGE,"E61"),sQuery(id+"F0.wireOp",EDGE,"E62"),sQuery(id+"F0.wireOp",EDGE,"E63"),sQuery(id+"F0.wireOp",EDGE,"E64"),sQuery(id+"F0.wireOp",EDGE,"E65"),sQuery(id+"F0.wireOp",EDGE,"E66"),sQuery(id+"F0.wireOp",EDGE,"E67"),sQuery(id+"F0.wireOp",EDGE,"E68"),sQuery(id+"F0.wireOp",EDGE,"E69"),sQuery(id+"F0.wireOp",EDGE,"E70"),sQuery(id+"F0.wireOp",EDGE,"E71"),sQuery(id+"F0.wireOp",EDGE,"E72"),sQuery(id+"F0.wireOp",EDGE,"E73"),sQuery(id+"F0.wireOp",EDGE,"E74"),sQuery(id+"F0.wireOp",EDGE,"E75"),sQuery(id+"F0.wireOp",EDGE,"E76"),sQuery(id+"F0.wireOp",EDGE,"E77"),sQuery(id+"F0.wireOp",EDGE,"E78"),sQuery(id+"F0.wireOp",EDGE,"E79"),sQuery(id+"F0.wireOp",EDGE,"E80"),sQuery(id+"F0.wireOp",EDGE,"E81"),sQuery(id+"F0.wireOp",EDGE,"E82"),sQuery(id+"F0.wireOp",EDGE,"E83"),sQuery(id+"F0.wireOp",EDGE,"E84"),sQuery(id+"F0.wireOp",EDGE,"E85"),sQuery(id+"F0.wireOp",EDGE,"E86"),sQuery(id+"F0.wireOp",EDGE,"E87"),sQuery(id+"F0.wireOp",EDGE,"E88"),sQuery(id+"F0.wireOp",EDGE,"E89"),sQuery(id+"F0.wireOp",EDGE,"E90"),sQuery(id+"F0.wireOp",EDGE,"E91"),sQuery(id+"F0.wireOp",EDGE,"E92"),sQuery(id+"F0.wireOp",EDGE,"E93"),sQuery(id+"F0.wireOp",EDGE,"E94"),sQuery(id+"F0.wireOp",EDGE,"E95"),sQuery(id+"F0.wireOp",EDGE,"E96"),sQuery(id+"F0.wireOp",EDGE,"E97"),sQuery(id+"F0.wireOp",EDGE,"E98"),sQuery(id+"F0.wireOp",EDGE,"E99"),sQuery(id+"F0.wireOp",EDGE,"E100"),sQuery(id+"F0.wireOp",EDGE,"E101"),sQuery(id+"F0.wireOp",EDGE,"E102"),sQuery(id+"F0.wireOp",EDGE,"E103"),sQuery(id+"F0.wireOp",EDGE,"E104"),sQuery(id+"F0.wireOp",EDGE,"E105"),sQuery(id+"F0.wireOp",EDGE,"E106"),sQuery(id+"F0.wireOp",EDGE,"E107"),sQuery(id+"F0.wireOp",EDGE,"E108"),sQuery(id+"F0.wireOp",EDGE,"E109"),sQuery(id+"F0.wireOp",EDGE,"E110"),sQuery(id+"F0.wireOp",EDGE,"E111"),sQuery(id+"F0.wireOp",EDGE,"E112"),sQuery(id+"F0.wireOp",EDGE,"E113"),sQuery(id+"F0.wireOp",EDGE,"E114"),sQuery(id+"F0.wireOp",EDGE,"E115"),sQuery(id+"F0.wireOp",EDGE,"E116"),sQuery(id+"F0.wireOp",EDGE,"E117"),sQuery(id+"F0.wireOp",EDGE,"E118"),sQuery(id+"F0.wireOp",EDGE,"E119"),sQuery(id+"F0.wireOp",EDGE,"E120"),sQuery(id+"F0.wireOp",EDGE,"E121"),sQuery(id+"F0.wireOp",EDGE,"E122"),sQuery(id+"F0.wireOp",EDGE,"E123"),sQuery(id+"F0.wireOp",EDGE,"E124"),sQuery(id+"F0.wireOp",EDGE,"E125"),sQuery(id+"F0.wireOp",EDGE,"E126"),sQuery(id+"F0.wireOp",EDGE,"E127"),sQuery(id+"F0.wireOp",EDGE,"E128"),sQuery(id+"F0.wireOp",EDGE,"E129"),sQuery(id+"F0.wireOp",EDGE,"E130"),sQuery(id+"F0.wireOp",EDGE,"E131"),sQuery(id+"F0.wireOp",EDGE,"E132"),sQuery(id+"F0.wireOp",EDGE,"E133"),sQuery(id+"F0.wireOp",EDGE,"E134"),sQuery(id+"F0.wireOp",EDGE,"E135"),sQuery(id+"F0.wireOp",EDGE,"E136"),sQuery(id+"F0.wireOp",EDGE,"E137"),sQuery(id+"F0.wireOp",EDGE,"E138"),sQuery(id+"F0.wireOp",EDGE,"E139"),sQuery(id+"F0.wireOp",EDGE,"E140"),sQuery(id+"F0.wireOp",EDGE,"E141"),sQuery(id+"F0.wireOp",EDGE,"E142"),sQuery(id+"F0.wireOp",EDGE,"E143"),sQuery(id+"F0.wireOp",EDGE,"E144"),sQuery(id+"F0.wireOp",EDGE,"E145"),sQuery(id+"F0.wireOp",EDGE,"E146"),sQuery(id+"F0.wireOp",EDGE,"E147"),sQuery(id+"F0.wireOp",EDGE,"E148"),sQuery(id+"F0.wireOp",EDGE,"E149"),sQuery(id+"F0.wireOp",EDGE,"E150"),sQuery(id+"F0.wireOp",EDGE,"E151"),sQuery(id+"F0.wireOp",EDGE,"E152"),sQuery(id+"F0.wireOp",EDGE,"E153"),sQuery(id+"F0.wireOp",EDGE,"E154"),sQuery(id+"F0.wireOp",EDGE,"E155"),sQuery(id+"F0.wireOp",EDGE,"E156"),sQuery(id+"F0.wireOp",EDGE,"E157"),sQuery(id+"F0.wireOp",EDGE,"E158"),sQuery(id+"F0.wireOp",EDGE,"E159"),sQuery(id+"F0.wireOp",EDGE,"E160"),sQuery(id+"F0.wireOp",EDGE,"E161"),sQuery(id+"F0.wireOp",EDGE,"E162"),sQuery(id+"F0.wireOp",EDGE,"E163"),sQuery(id+"F0.wireOp",EDGE,"E164"),sQuery(id+"F0.wireOp",EDGE,"E165"),sQuery(id+"F0.wireOp",EDGE,"E166"),sQuery(id+"F0.wireOp",EDGE,"E167"),sQuery(id+"F0.wireOp",EDGE,"E168"),sQuery(id+"F0.wireOp",EDGE,"E169"),sQuery(id+"F0.wireOp",EDGE,"E170"),sQuery(id+"F0.wireOp",EDGE,"E171"),sQuery(id+"F0.wireOp",EDGE,"E172"),sQuery(id+"F0.wireOp",EDGE,"E173"),sQuery(id+"F0.wireOp",EDGE,"E174"),sQuery(id+"F0.wireOp",EDGE,"E175"),sQuery(id+"F0.wireOp",EDGE,"E176"),sQuery(id+"F0.wireOp",EDGE,"E177"),sQuery(id+"F0.wireOp",EDGE,"E178"),sQuery(id+"F0.wireOp",EDGE,"E179"),sQuery(id+"F0.wireOp",EDGE,"E180"),sQuery(id+"F0.wireOp",EDGE,"E181"),sQuery(id+"F0.wireOp",EDGE,"E182"),sQuery(id+"F0.wireOp",EDGE,"E183"),sQuery(id+"F0.wireOp",EDGE,"E184"),sQuery(id+"F0.wireOp",EDGE,"E185"),sQuery(id+"F0.wireOp",EDGE,"E186"),sQuery(id+"F0.wireOp",EDGE,"E187"),sQuery(id+"F0.wireOp",EDGE,"E188"),sQuery(id+"F0.wireOp",EDGE,"E189"),sQuery(id+"F0.wireOp",EDGE,"E190"),sQuery(id+"F0.wireOp",EDGE,"E191"),sQuery(id+"F0.wireOp",EDGE,"E192"),sQuery(id+"F0.wireOp",EDGE,"E193"),sQuery(id+"F0.wireOp",EDGE,"E194"),sQuery(id+"F0.wireOp",EDGE,"E195"),sQuery(id+"F0.wireOp",EDGE,"E196"),sQuery(id+"F0.wireOp",EDGE,"E197"),sQuery(id+"F0.wireOp",EDGE,"E198"),sQuery(id+"F0.wireOp",EDGE,"E199"),sQuery(id+"F0.wireOp",EDGE,"E200"),sQuery(id+"F0.wireOp",EDGE,"E201"),sQuery(id+"F0.wireOp",EDGE,"E202"),sQuery(id+"F0.wireOp",EDGE,"E203"),sQuery(id+"F0.wireOp",EDGE,"E204"),sQuery(id+"F0.wireOp",EDGE,"E205"),sQuery(id+"F0.wireOp",EDGE,"E206"),sQuery(id+"F0.wireOp",EDGE,"E207"),sQuery(id+"F0.wireOp",EDGE,"E208"),sQuery(id+"F0.wireOp",EDGE,"E209"),sQuery(id+"F0.wireOp",EDGE,"E210"),sQuery(id+"F0.wireOp",EDGE,"E211"),sQuery(id+"F0.wireOp",EDGE,"E212"),sQuery(id+"F0.wireOp",EDGE,"E213"),sQuery(id+"F0.wireOp",EDGE,"E214"),sQuery(id+"F0.wireOp",EDGE,"E215"),sQuery(id+"F0.wireOp",EDGE,"E216"),sQuery(id+"F0.wireOp",EDGE,"E217"),sQuery(id+"F0.wireOp",EDGE,"E218"),sQuery(id+"F0.wireOp",EDGE,"E219"),sQuery(id+"F0.wireOp",EDGE,"E220"),sQuery(id+"F0.wireOp",EDGE,"E221"),sQuery(id+"F0.wireOp",EDGE,"E222"),sQuery(id+"F0.wireOp",EDGE,"E223"),sQuery(id+"F0.wireOp",EDGE,"E224"),sQuery(id+"F0.wireOp",EDGE,"E225"),sQuery(id+"F0.wireOp",EDGE,"E226"),sQuery(id+"F0.wireOp",EDGE,"E227"),sQuery(id+"F0.wireOp",EDGE,"E228"),sQuery(id+"F0.wireOp",EDGE,"E229"),sQuery(id+"F0.wireOp",EDGE,"E230"),sQuery(id+"F0.wireOp",EDGE,"E231"),sQuery(id+"F0.wireOp",EDGE,"E232"),sQuery(id+"F0.wireOp",EDGE,"E233"),sQuery(id+"F0.wireOp",EDGE,"E234"),sQuery(id+"F0.wireOp",EDGE,"E235"),sQuery(id+"F0.wireOp",EDGE,"E236"),sQuery(id+"F0.wireOp",EDGE,"E237"),sQuery(id+"F0.wireOp",EDGE,"E238"),sQuery(id+"F0.wireOp",EDGE,"E239"),sQuery(id+"F0.wireOp",EDGE,"E240"),sQuery(id+"F0.wireOp",EDGE,"E241"),sQuery(id+"F0.wireOp",EDGE,"E242"),sQuery(id+"F0.wireOp",EDGE,"E243"),sQuery(id+"F0.wireOp",EDGE,"E244"),sQuery(id+"F0.wireOp",EDGE,"E245"),sQuery(id+"F0.wireOp",EDGE,"E246"),sQuery(id+"F0.wireOp",EDGE,"E247"),sQuery(id+"F0.wireOp",EDGE,"E248"),sQuery(id+"F0.wireOp",EDGE,"E249"),sQuery(id+"F0.wireOp",EDGE,"E250"),sQuery(id+"F0.wireOp",EDGE,"E251"),sQuery(id+"F0.wireOp",EDGE,"E252"),sQuery(id+"F0.wireOp",EDGE,"E253"),sQuery(id+"F0.wireOp",EDGE,"E254"),sQuery(id+"F0.wireOp",EDGE,"E255"),sQuery(id+"F0.wireOp",EDGE,"E256"),sQuery(id+"F0.wireOp",EDGE,"E257"),sQuery(id+"F0.wireOp",EDGE,"E258"),sQuery(id+"F0.wireOp",EDGE,"E259"),sQuery(id+"F0.wireOp",EDGE,"E260"),sQuery(id+"F0.wireOp",EDGE,"E261"),sQuery(id+"F0.wireOp",EDGE,"E262"),sQuery(id+"F0.wireOp",EDGE,"E263"),sQuery(id+"F0.wireOp",EDGE,"E264"),sQuery(id+"F0.wireOp",EDGE,"E265"),sQuery(id+"F0.wireOp",EDGE,"E266"),sQuery(id+"F0.wireOp",EDGE,"E267"),sQuery(id+"F0.wireOp",EDGE,"E268"),sQuery(id+"F0.wireOp",EDGE,"E269"),sQuery(id+"F0.wireOp",EDGE,"E270"),sQuery(id+"F0.wireOp",EDGE,"E271"),sQuery(id+"F0.wireOp",EDGE,"E272"),sQuery(id+"F0.wireOp",EDGE,"E273"),sQuery(id+"F0.wireOp",EDGE,"E274"),sQuery(id+"F0.wireOp",EDGE,"E275"),sQuery(id+"F0.wireOp",EDGE,"E276"),sQuery(id+"F0.wireOp",EDGE,"E277"),sQuery(id+"F0.wireOp",EDGE,"E278"),sQuery(id+"F0.wireOp",EDGE,"E279"),sQuery(id+"F0.wireOp",EDGE,"E280"),sQuery(id+"F0.wireOp",EDGE,"E281"),sQuery(id+"F0.wireOp",EDGE,"E282"),sQuery(id+"F0.wireOp",EDGE,"E283"),sQuery(id+"F0.wireOp",EDGE,"E284"),sQuery(id+"F0.wireOp",EDGE,"E285"),sQuery(id+"F0.wireOp",EDGE,"E286"),sQuery(id+"F0.wireOp",EDGE,"E287"),sQuery(id+"F0.wireOp",EDGE,"E288"),sQuery(id+"F0.wireOp",EDGE,"E289"),sQuery(id+"F0.wireOp",EDGE,"E290"),sQuery(id+"F0.wireOp",EDGE,"E291"),sQuery(id+"F0.wireOp",EDGE,"E292"),sQuery(id+"F0.wireOp",EDGE,"E293"),sQuery(id+"F0.wireOp",EDGE,"E294"),sQuery(id+"F0.wireOp",EDGE,"E295"),sQuery(id+"F0.wireOp",EDGE,"E296"),sQuery(id+"F0.wireOp",EDGE,"E297"),sQuery(id+"F0.wireOp",EDGE,"E298"),sQuery(id+"F0.wireOp",EDGE,"E299"),sQuery(id+"F0.wireOp",EDGE,"E300"),sQuery(id+"F0.wireOp",EDGE,"E301"),sQuery(id+"F0.wireOp",EDGE,"E302"),sQuery(id+"F0.wireOp",EDGE,"E303"),sQuery(id+"F0.wireOp",EDGE,"E304"),sQuery(id+"F0.wireOp",EDGE,"E305"),sQuery(id+"F0.wireOp",EDGE,"E306"),sQuery(id+"F0.wireOp",EDGE,"E307"),sQuery(id+"F0.wireOp",EDGE,"E308"),sQuery(id+"F0.wireOp",EDGE,"E309"),sQuery(id+"F0.wireOp",EDGE,"E310"),sQuery(id+"F0.wireOp",EDGE,"E311"),sQuery(id+"F0.wireOp",EDGE,"E312"),sQuery(id+"F0.wireOp",EDGE,"E313"),sQuery(id+"F0.wireOp",EDGE,"E314"),sQuery(id+"F0.wireOp",EDGE,"E315"),sQuery(id+"F0.wireOp",EDGE,"E316"),sQuery(id+"F0.wireOp",EDGE,"E317"),sQuery(id+"F0.wireOp",EDGE,"E318"),sQuery(id+"F0.wireOp",EDGE,"E319"),sQuery(id+"F0.wireOp",EDGE,"E320"),sQuery(id+"F0.wireOp",EDGE,"E321"),sQuery(id+"F0.wireOp",EDGE,"E322"),sQuery(id+"F0.wireOp",EDGE,"E323"),sQuery(id+"F0.wireOp",EDGE,"E324"),sQuery(id+"F0.wireOp",EDGE,"E325"),sQuery(id+"F0.wireOp",EDGE,"E326"),sQuery(id+"F0.wireOp",EDGE,"E327"),sQuery(id+"F0.wireOp",EDGE,"E328"),sQuery(id+"F0.wireOp",EDGE,"E329"),sQuery(id+"F0.wireOp",EDGE,"E330"),sQuery(id+"F0.wireOp",EDGE,"E331"),sQuery(id+"F0.wireOp",EDGE,"E332"),sQuery(id+"F0.wireOp",EDGE,"E333"),sQuery(id+"F0.wireOp",EDGE,"E334"),sQuery(id+"F0.wireOp",EDGE,"E335"),sQuery(id+"F0.wireOp",EDGE,"E336"),sQuery(id+"F0.wireOp",EDGE,"E337"),sQuery(id+"F0.wireOp",EDGE,"E338"),sQuery(id+"F0.wireOp",EDGE,"E339"),sQuery(id+"F0.wireOp",EDGE,"E340"),sQuery(id+"F0.wireOp",EDGE,"E341"),sQuery(id+"F0.wireOp",EDGE,"E342"),sQuery(id+"F0.wireOp",EDGE,"E343"),sQuery(id+"F0.wireOp",EDGE,"E344"),sQuery(id+"F0.wireOp",EDGE,"E345"),sQuery(id+"F0.wireOp",EDGE,"E346"),sQuery(id+"F0.wireOp",EDGE,"E347"),sQuery(id+"F0.wireOp",EDGE,"E348"),sQuery(id+"F0.wireOp",EDGE,"E349"),sQuery(id+"F0.wireOp",EDGE,"E350"),sQuery(id+"F0.wireOp",EDGE,"E351"),sQuery(id+"F0.wireOp",EDGE,"E352"),sQuery(id+"F0.wireOp",EDGE,"E353"),sQuery(id+"F0.wireOp",EDGE,"E354"),sQuery(id+"F0.wireOp",EDGE,"E355"),sQuery(id+"F0.wireOp",EDGE,"E356"),sQuery(id+"F0.wireOp",EDGE,"E357"),sQuery(id+"F0.wireOp",EDGE,"E358"),sQuery(id+"F0.wireOp",EDGE,"E359"),sQuery(id+"F0.wireOp",EDGE,"E360"),sQuery(id+"F0.wireOp",EDGE,"E361"),sQuery(id+"F0.wireOp",EDGE,"E362"),sQuery(id+"F0.wireOp",EDGE,"E363"),sQuery(id+"F0.wireOp",EDGE,"E364"),sQuery(id+"F0.wireOp",EDGE,"E365"),sQuery(id+"F0.wireOp",EDGE,"E366"),sQuery(id+"F0.wireOp",EDGE,"E367"),sQuery(id+"F0.wireOp",EDGE,"E368"),sQuery(id+"F0.wireOp",EDGE,"E369"),sQuery(id+"F0.wireOp",EDGE,"E370"),sQuery(id+"F0.wireOp",EDGE,"E371"),sQuery(id+"F0.wireOp",EDGE,"E372"),sQuery(id+"F0.wireOp",EDGE,"E373"),sQuery(id+"F0.wireOp",EDGE,"E374"),sQuery(id+"F0.wireOp",EDGE,"E375"),sQuery(id+"F0.wireOp",EDGE,"E376"),sQuery(id+"F0.wireOp",EDGE,"E377"),sQuery(id+"F0.wireOp",EDGE,"E378"),sQuery(id+"F0.wireOp",EDGE,"E379"),sQuery(id+"F0.wireOp",EDGE,"E380"),sQuery(id+"F0.wireOp",EDGE,"E381"),sQuery(id+"F0.wireOp",EDGE,"E382"),sQuery(id+"F0.wireOp",EDGE,"E383"),sQuery(id+"F0.wireOp",EDGE,"E384"),sQuery(id+"F0.wireOp",EDGE,"E385"),sQuery(id+"F0.wireOp",EDGE,"E386"),sQuery(id+"F0.wireOp",EDGE,"E387"),sQuery(id+"F0.wireOp",EDGE,"E388"),sQuery(id+"F0.wireOp",EDGE,"E389"),sQuery(id+"F0.wireOp",EDGE,"E390"),sQuery(id+"F0.wireOp",EDGE,"E391"),sQuery(id+"F0.wireOp",EDGE,"E392"),sQuery(id+"F0.wireOp",EDGE,"E393"),sQuery(id+"F0.wireOp",EDGE,"E394"),sQuery(id+"F0.wireOp",EDGE,"E395"),sQuery(id+"F0.wireOp",EDGE,"E396"),sQuery(id+"F0.wireOp",EDGE,"E397"),sQuery(id+"F0.wireOp",EDGE,"E398"),sQuery(id+"F0.wireOp",EDGE,"E399"),sQuery(id+"F0.wireOp",EDGE,"E400"),sQuery(id+"F0.wireOp",EDGE,"E401"),sQuery(id+"F0.wireOp",EDGE,"E402"),sQuery(id+"F0.wireOp",EDGE,"E403"),sQuery(id+"F0.wireOp",EDGE,"E404"),sQuery(id+"F0.wireOp",EDGE,"E405"),sQuery(id+"F0.wireOp",EDGE,"E406"),sQuery(id+"F0.wireOp",EDGE,"E407"),sQuery(id+"F0.wireOp",EDGE,"E408"),sQuery(id+"F0.wireOp",EDGE,"E409"),sQuery(id+"F0.wireOp",EDGE,"E410"),sQuery(id+"F0.wireOp",EDGE,"E411"),sQuery(id+"F0.wireOp",EDGE,"E412"),sQuery(id+"F0.wireOp",EDGE,"E413"),sQuery(id+"F0.wireOp",EDGE,"E414"),sQuery(id+"F0.wireOp",EDGE,"E415"),sQuery(id+"F0.wireOp",EDGE,"E416"),sQuery(id+"F0.wireOp",EDGE,"E417"),sQuery(id+"F0.wireOp",EDGE,"E418"),sQuery(id+"F0.wireOp",EDGE,"E419"),sQuery(id+"F0.wireOp",EDGE,"E420"),sQuery(id+"F0.wireOp",EDGE,"E421"),sQuery(id+"F0.wireOp",EDGE,"E422"),sQuery(id+"F0.wireOp",EDGE,"E423"),sQuery(id+"F0.wireOp",EDGE,"E424"),sQuery(id+"F0.wireOp",EDGE,"E425"),sQuery(id+"F0.wireOp",EDGE,"E426"),sQuery(id+"F0.wireOp",EDGE,"E427"),sQuery(id+"F0.wireOp",EDGE,"E428"),sQuery(id+"F0.wireOp",EDGE,"E429"),sQuery(id+"F0.wireOp",EDGE,"E430"),sQuery(id+"F0.wireOp",EDGE,"E431"),sQuery(id+"F0.wireOp",EDGE,"E432"),sQuery(id+"F0.wireOp",EDGE,"E433"),sQuery(id+"F0.wireOp",EDGE,"E434"),sQuery(id+"F0.wireOp",EDGE,"E435"),sQuery(id+"F0.wireOp",EDGE,"E436"),sQuery(id+"F0.wireOp",EDGE,"E437"),sQuery(id+"F0.wireOp",EDGE,"E438"),sQuery(id+"F0.wireOp",EDGE,"E439"),sQuery(id+"F0.wireOp",EDGE,"E440"),sQuery(id+"F0.wireOp",EDGE,"E441"),sQuery(id+"F0.wireOp",EDGE,"E442"),sQuery(id+"F0.wireOp",EDGE,"E443"),sQuery(id+"F0.wireOp",EDGE,"E444"),sQuery(id+"F0.wireOp",EDGE,"E445"),sQuery(id+"F0.wireOp",EDGE,"E446"),sQuery(id+"F0.wireOp",EDGE,"E447"),sQuery(id+"F0.wireOp",EDGE,"E448"),sQuery(id+"F0.wireOp",EDGE,"E449"),sQuery(id+"F0.wireOp",EDGE,"E450"),sQuery(id+"F0.wireOp",EDGE,"E451"),sQuery(id+"F0.wireOp",EDGE,"E452"),sQuery(id+"F0.wireOp",EDGE,"E453"),sQuery(id+"F0.wireOp",EDGE,"E454"),sQuery(id+"F0.wireOp",EDGE,"E455"),sQuery(id+"F0.wireOp",EDGE,"E456"),sQuery(id+"F0.wireOp",EDGE,"E457"),sQuery(id+"F0.wireOp",EDGE,"E458"),sQuery(id+"F0.wireOp",EDGE,"E459"),sQuery(id+"F0.wireOp",EDGE,"E460"),sQuery(id+"F0.wireOp",EDGE,"E461"),sQuery(id+"F0.wireOp",EDGE,"E462"),sQuery(id+"F0.wireOp",EDGE,"E463"),sQuery(id+"F0.wireOp",EDGE,"E464"),sQuery(id+"F0.wireOp",EDGE,"E465"),sQuery(id+"F0.wireOp",EDGE,"E466"),sQuery(id+"F0.wireOp",EDGE,"E467"),sQuery(id+"F0.wireOp",EDGE,"E468"),sQuery(id+"F0.wireOp",EDGE,"E469"),sQuery(id+"F0.wireOp",EDGE,"E470"),sQuery(id+"F0.wireOp",EDGE,"E471"),sQuery(id+"F0.wireOp",EDGE,"E472"),sQuery(id+"F0.wireOp",EDGE,"E473"),sQuery(id+"F0.wireOp",EDGE,"E474"),sQuery(id+"F0.wireOp",EDGE,"E475"),sQuery(id+"F0.wireOp",EDGE,"E476"),sQuery(id+"F0.wireOp",EDGE,"E477"),sQuery(id+"F0.wireOp",EDGE,"E478"),sQuery(id+"F0.wireOp",EDGE,"E479"),sQuery(id+"F0.wireOp",EDGE,"E480"),sQuery(id+"F0.wireOp",EDGE,"E481"),sQuery(id+"F0.wireOp",EDGE,"E482"),sQuery(id+"F0.wireOp",EDGE,"E483"),sQuery(id+"F0.wireOp",EDGE,"E484"),sQuery(id+"F0.wireOp",EDGE,"E485"),sQuery(id+"F0.wireOp",EDGE,"E486"),sQuery(id+"F0.wireOp",EDGE,"E487"),sQuery(id+"F0.wireOp",EDGE,"E488"),sQuery(id+"F0.wireOp",EDGE,"E489.0"),sQuery(id+"F0.wireOp",EDGE,"E489.1"),sQuery(id+"F0.wireOp",EDGE,"E489.2"),sQuery(id+"F0.wireOp",EDGE,"E489.3"),sQuery(id+"F0.wireOp",EDGE,"E489.4"),sQuery(id+"F0.wireOp",EDGE,"E489.5"),sQuery(id+"F0.wireOp",EDGE,"E490"),sQuery(id+"F0.wireOp",EDGE,"E491"),sQuery(id+"F0.wireOp",EDGE,"E493"),sQuery(id+"F0.wireOp",EDGE,"E494"),sQuery(id+"F0.wireOp",EDGE,"E495"),sQuery(id+"F0.wireOp",EDGE,"E496"),sQuery(id+"F0.wireOp",EDGE,"E497"),sQuery(id+"F0.wireOp",EDGE,"E499"),sQuery(id+"F0.wireOp",EDGE,"E500"),sQuery(id+"F0.wireOp",EDGE,"E501"),sQuery(id+"F0.wireOp",EDGE,"E502"),sQuery(id+"F0.wireOp",EDGE,"E504.bottom"),sQuery(id+"F0.wireOp",EDGE,"E504.top"),sQuery(id+"F0.wireOp",EDGE,"E504.left"),sQuery(id+"F0.wireOp",EDGE,"E504.right"),sQuery(id+"F0.wireOp",EDGE,"E505.bottom"),sQuery(id+"F0.wireOp",EDGE,"E505.top"),sQuery(id+"F0.wireOp",EDGE,"E505.left"),sQuery(id+"F0.wireOp",EDGE,"E505.right"),sQuery(id+"F0.wireOp",EDGE,"E506"),sQuery(id+"F0.wireOp",EDGE,"E507"),sQuery(id+"F0.wireOp",EDGE,"E508"),sQuery(id+"F0.wireOp",EDGE,"E509"),sQuery(id+"F0.wireOp",EDGE,"E510"),sQuery(id+"F0.wireOp",EDGE,"E513"),sQuery(id+"F0.wireOp",EDGE,"E514"),sQuery(id+"F0.wireOp",EDGE,"E516"),sQuery(id+"F0.wireOp",EDGE,"E517"),sQuery(id+"F0.wireOp",EDGE,"E519"),sQuery(id+"F0.wireOp",EDGE,"E520"),sQuery(id+"F0.wireOp",EDGE,"E521"),sQuery(id+"F0.wireOp",EDGE,"E522")])]});
            transform(context, id + "F5", {"entities" : qUnion([Q0]), "transformType" : TransformType.TRANSLATION_3D, "dx" : 6.35 * mm, "dy" : 0 * mm, "dz" : -10.16 * mm, "makeCopy" : false});
        }
        {
            var Q0;
            {var subQ0=sQuery(id+"F0.wireOp",EDGE,"E489.5");var subQ1=makeQuery(id+"F0.imprint","IMPRINT",VERTEX,{"disambiguationData":[OD(0.0)],"derivedFrom":subQ0});var subQ2=makeQuery(id+"F0.imprint","IMPRINT",VERTEX,{"disambiguationData":[OD(1.0)],"derivedFrom":subQ0});Q0=makeQuery(id+"F3.boolean.opBoolean","MERGE",EDGE,{"derivedFrom":[makeQuery(id+"F1.opExtrude","CAP_EDGE",EDGE,{"disambiguationData":[OSD([subQ0]),TDD([makeQuery(id+"F0.imprint","IMPRINT",EDGE,{"disambiguationData":[TD([[subQ2,1.0]])],"derivedFrom":subQ0}),makeQuery(id+"F0.imprint","IMPRINT",EDGE,{"disambiguationData":[TD([[subQ2,-1.0]])],"derivedFrom":subQ0})])],"isStart":true}),makeQuery(id+"F1.opExtrude","CAP_EDGE",EDGE,{"disambiguationData":[OSD([subQ0]),TDD([makeQuery(id+"F0.imprint","IMPRINT",EDGE,{"disambiguationData":[TD([[subQ1,1.0]])],"derivedFrom":subQ0}),makeQuery(id+"F0.imprint","IMPRINT",EDGE,{"disambiguationData":[TD([[subQ1,-1.0]])],"derivedFrom":subQ0})])],"isStart":true}),makeQuery(id+"F3.opExtrude","CAP_EDGE",EDGE,{"disambiguationData":[OSD([subQ0])],"isStart":true})]});}
            var Q1;
            Q1=makeQuery(id+"F1.opExtrude","CAP_EDGE",EDGE,{"disambiguationData":[OSD([sQuery(id+"F0.wireOp",EDGE,"E489.0")])],"isStart":true});
            var Q2;
            {var subQ0=sQuery(id+"F0.wireOp",EDGE,"E489.1");var subQ1=makeQuery(id+"F0.imprint","IMPRINT",VERTEX,{"disambiguationData":[OD(1.0)],"derivedFrom":subQ0});var subQ2=makeQuery(id+"F0.imprint","IMPRINT",VERTEX,{"disambiguationData":[OD(0.0)],"derivedFrom":subQ0});Q2=makeQuery(id+"F3.boolean.opBoolean","MERGE",EDGE,{"derivedFrom":[makeQuery(id+"F1.opExtrude","CAP_EDGE",EDGE,{"disambiguationData":[OSD([subQ0]),TDD([makeQuery(id+"F0.imprint","IMPRINT",EDGE,{"disambiguationData":[TD([[subQ2,1.0]])],"derivedFrom":subQ0}),makeQuery(id+"F0.imprint","IMPRINT",EDGE,{"disambiguationData":[TD([[subQ2,-1.0]])],"derivedFrom":subQ0})])],"isStart":true}),makeQuery(id+"F1.opExtrude","CAP_EDGE",EDGE,{"disambiguationData":[OSD([subQ0]),TDD([makeQuery(id+"F0.imprint","IMPRINT",EDGE,{"disambiguationData":[TD([[subQ1,1.0]])],"derivedFrom":subQ0}),makeQuery(id+"F0.imprint","IMPRINT",EDGE,{"disambiguationData":[TD([[subQ1,-1.0]])],"derivedFrom":subQ0})])],"isStart":true}),makeQuery(id+"F3.opExtrude","CAP_EDGE",EDGE,{"disambiguationData":[OSD([subQ0])],"isStart":true})]});}
            var Q3;
            Q3=makeQuery(id+"F1.opExtrude","CAP_EDGE",EDGE,{"disambiguationData":[OSD([sQuery(id+"F0.wireOp",EDGE,"E489.2")])],"isStart":true});
            var Q4;
            Q4=makeQuery(id+"F1.opExtrude","CAP_EDGE",EDGE,{"disambiguationData":[OSD([sQuery(id+"F0.wireOp",EDGE,"E489.4")])],"isStart":true});
            var Q5;
            {var subQ0=sQuery(id+"F0.wireOp",EDGE,"E489.3");var subQ1=makeQuery(id+"F0.imprint","IMPRINT",VERTEX,{"disambiguationData":[OD(0.0)],"derivedFrom":subQ0});var subQ2=makeQuery(id+"F0.imprint","IMPRINT",VERTEX,{"disambiguationData":[OD(1.0)],"derivedFrom":subQ0});Q5=makeQuery(id+"F3.boolean.opBoolean","MERGE",EDGE,{"derivedFrom":[makeQuery(id+"F1.opExtrude","CAP_EDGE",EDGE,{"disambiguationData":[OSD([subQ0]),TDD([makeQuery(id+"F0.imprint","IMPRINT",EDGE,{"disambiguationData":[TD([[subQ2,1.0]])],"derivedFrom":subQ0}),makeQuery(id+"F0.imprint","IMPRINT",EDGE,{"disambiguationData":[TD([[subQ2,-1.0]])],"derivedFrom":subQ0})])],"isStart":true}),makeQuery(id+"F1.opExtrude","CAP_EDGE",EDGE,{"disambiguationData":[OSD([subQ0]),TDD([makeQuery(id+"F0.imprint","IMPRINT",EDGE,{"disambiguationData":[TD([[subQ1,1.0]])],"derivedFrom":subQ0}),makeQuery(id+"F0.imprint","IMPRINT",EDGE,{"disambiguationData":[TD([[subQ1,-1.0]])],"derivedFrom":subQ0})])],"isStart":true}),makeQuery(id+"F3.opExtrude","CAP_EDGE",EDGE,{"disambiguationData":[OSD([subQ0])],"isStart":true})]});}
            chamfer(context, id + "F6", {"entities" : qUnion([Q0, Q1, Q2, Q3, Q4, Q5]), "chamferType" : ChamferType.TWO_OFFSETS, "width1" : 3.05 * mm, "oppositeDirection" : true, "width2" : 9.52 * mm, "tangentPropagation" : true});
        }
        {
            var Q0;
            {var subQ0=sQuery(id+"F0.wireOp",EDGE,"E489.0");Q0=makeQuery(id+"F6.opChamfer","BLEND_EDGE",EDGE,{"blendedFrom":[makeQuery(id+"F1.opExtrude","CAP_EDGE",EDGE,{"disambiguationData":[OSD([subQ0])],"isStart":true}),makeQuery(id+"F1.opExtrude","SWEPT_FACE",FACE,{"disambiguationData":[OSD([subQ0])]})],"blendedInto":[makeQuery(id+"F1.opExtrude","SWEPT_FACE",FACE,{"disambiguationData":[OSD([subQ0])]})]});}
            var Q1;
            {var subQ0=sQuery(id+"F0.wireOp",EDGE,"E489.2");Q1=makeQuery(id+"F6.opChamfer","BLEND_EDGE",EDGE,{"blendedFrom":[makeQuery(id+"F1.opExtrude","CAP_EDGE",EDGE,{"disambiguationData":[OSD([subQ0])],"isStart":true}),makeQuery(id+"F1.opExtrude","SWEPT_FACE",FACE,{"disambiguationData":[OSD([subQ0])]})],"blendedInto":[makeQuery(id+"F1.opExtrude","SWEPT_FACE",FACE,{"disambiguationData":[OSD([subQ0])]})]});}
            var Q2;
            {var subQ0=sQuery(id+"F0.wireOp",EDGE,"E489.4");Q2=makeQuery(id+"F6.opChamfer","BLEND_EDGE",EDGE,{"blendedFrom":[makeQuery(id+"F1.opExtrude","CAP_EDGE",EDGE,{"disambiguationData":[OSD([subQ0])],"isStart":true}),makeQuery(id+"F1.opExtrude","SWEPT_FACE",FACE,{"disambiguationData":[OSD([subQ0])]})],"blendedInto":[makeQuery(id+"F1.opExtrude","SWEPT_FACE",FACE,{"disambiguationData":[OSD([subQ0])]})]});}
            chamfer(context, id + "F7", {"entities" : qUnion([Q0, Q1, Q2]), "width" : 5.08 * mm, "tangentPropagation" : true});
        }
        {
            var Q0;
            Q0=makeQuery(id+"F1.opExtrude","CAP_EDGE",EDGE,{"disambiguationData":[OSD([sQuery(id+"F0.wireOp",EDGE,"E505.top")])],"isStart":true});
            var Q1;
            Q1=makeQuery(id+"F1.opExtrude","CAP_EDGE",EDGE,{"disambiguationData":[OSD([sQuery(id+"F0.wireOp",EDGE,"E505.left")])],"isStart":true});
            var Q2;
            Q2=makeQuery(id+"F1.opExtrude","CAP_EDGE",EDGE,{"disambiguationData":[OSD([sQuery(id+"F0.wireOp",EDGE,"E505.bottom")])],"isStart":true});
            var Q3;
            Q3=makeQuery(id+"F1.opExtrude","CAP_EDGE",EDGE,{"disambiguationData":[OSD([sQuery(id+"F0.wireOp",EDGE,"E505.right")])],"isStart":true});
            var Q4;
            Q4=makeQuery(id+"F1.opExtrude","CAP_EDGE",EDGE,{"disambiguationData":[OSD([sQuery(id+"F0.wireOp",EDGE,"E504.top")])],"isStart":true});
            var Q5;
            Q5=makeQuery(id+"F1.opExtrude","CAP_EDGE",EDGE,{"disambiguationData":[OSD([sQuery(id+"F0.wireOp",EDGE,"E504.left")])],"isStart":true});
            var Q6;
            Q6=makeQuery(id+"F1.opExtrude","CAP_EDGE",EDGE,{"disambiguationData":[OSD([sQuery(id+"F0.wireOp",EDGE,"E504.bottom")])],"isStart":true});
            var Q7;
            Q7=makeQuery(id+"F1.opExtrude","CAP_EDGE",EDGE,{"disambiguationData":[OSD([sQuery(id+"F0.wireOp",EDGE,"E504.right")])],"isStart":true});
            chamfer(context, id + "F8", {"entities" : qUnion([Q0, Q1, Q2, Q3, Q4, Q5, Q6, Q7]), "width" : 0.32 * mm, "tangentPropagation" : true});
        }
    });
